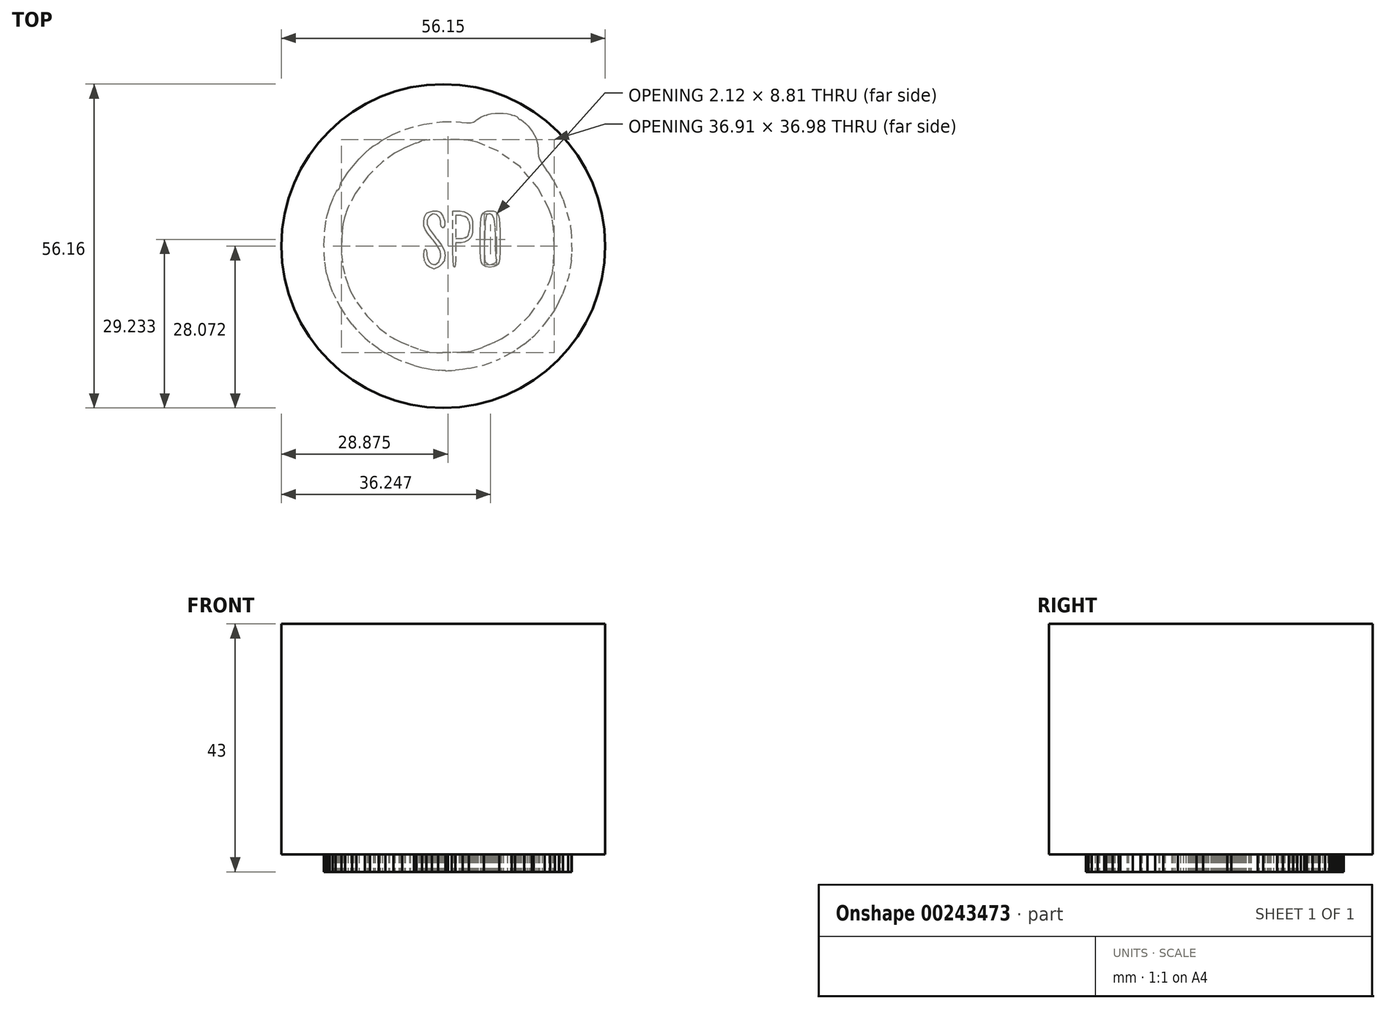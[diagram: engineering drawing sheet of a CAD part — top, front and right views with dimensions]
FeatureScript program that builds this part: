
annotation { "Feature Type Name" : "Feature", "Feature Type Description" : "" }
export const myFeature = defineFeature(function(context is Context, id is Id, definition is map)
    precondition{}
    {
        {
            var Q0;
            Q0=qCreatedBy(makeId("Top.planeOp"),FACE);
            var sketch = newSketch(context, id + "F0", { "sketchPlane" : qUnion([Q0])});
            skLineSegment(sketch, "E0", {"start": v(-1.98, -21.51) * mm, "end": v(-2.83, -21.44) * mm});
            skLineSegment(sketch, "E1", {"start": v(-2.83, -21.44) * mm, "end": v(-5.33, -20.94) * mm});
            skLineSegment(sketch, "E2", {"start": v(-5.33, -20.94) * mm, "end": v(-8.48, -19.86) * mm});
            skLineSegment(sketch, "E3", {"start": v(-8.48, -19.86) * mm, "end": v(-11.41, -18.31) * mm});
            skLineSegment(sketch, "E4", {"start": v(-11.41, -18.31) * mm, "end": v(-14.06, -16.34) * mm});
            skLineSegment(sketch, "E5", {"start": v(-14.06, -16.34) * mm, "end": v(-16.4, -13.97) * mm});
            skLineSegment(sketch, "E6", {"start": v(-16.4, -13.97) * mm, "end": v(-18.36, -11.25) * mm});
            skLineSegment(sketch, "E7", {"start": v(-18.36, -11.25) * mm, "end": v(-19.92, -8.21) * mm});
            skLineSegment(sketch, "E8", {"start": v(-19.92, -8.21) * mm, "end": v(-20.82, -5.74) * mm});
            skLineSegment(sketch, "E9", {"start": v(-20.82, -5.74) * mm, "end": v(-21.03, -4.9) * mm});
            skLineSegment(sketch, "E10", {"start": v(-21.03, -4.9) * mm, "end": v(-21.18, -4.33) * mm});
            skLineSegment(sketch, "E11", {"start": v(-21.18, -4.33) * mm, "end": v(-21.41, -2.57) * mm});
            skLineSegment(sketch, "E12", {"start": v(-21.41, -2.57) * mm, "end": v(-21.52, 0.18) * mm});
            skLineSegment(sketch, "E13", {"start": v(-21.52, 0.18) * mm, "end": v(-21.37, 2.94) * mm});
            skLineSegment(sketch, "E14", {"start": v(-21.37, 2.94) * mm, "end": v(-21.1, 4.72) * mm});
            skLineSegment(sketch, "E15", {"start": v(-21.1, 4.72) * mm, "end": v(-20.95, 5.3) * mm});
            skLineSegment(sketch, "E16", {"start": v(-20.95, 5.3) * mm, "end": v(-20.84, 5.71) * mm});
            skLineSegment(sketch, "E17", {"start": v(-20.84, 5.71) * mm, "end": v(-20.44, 6.97) * mm});
            skLineSegment(sketch, "E18", {"start": v(-20.44, 6.97) * mm, "end": v(-19.9, 8.4) * mm});
            skLineSegment(sketch, "E19", {"start": v(-19.9, 8.4) * mm, "end": v(-19.4, 9.41) * mm});
            skLineSegment(sketch, "E20", {"start": v(-19.4, 9.41) * mm, "end": v(-19.14, 9.79) * mm});
            skLineSegment(sketch, "E21", {"start": v(-19.14, 9.79) * mm, "end": v(-19.05, 9.79) * mm});
            skLineSegment(sketch, "E22", {"start": v(-19.05, 9.79) * mm, "end": v(-19, 9.79) * mm});
            skLineSegment(sketch, "E23", {"start": v(-19, 9.79) * mm, "end": v(-18.86, 9.93) * mm});
            skLineSegment(sketch, "E24", {"start": v(-18.86, 9.93) * mm, "end": v(-18.79, 10.18) * mm});
            skLineSegment(sketch, "E25", {"start": v(-18.79, 10.18) * mm, "end": v(-18.79, 10.27) * mm});
            skLineSegment(sketch, "E26", {"start": v(-18.79, 10.27) * mm, "end": v(-18.79, 10.42) * mm});
            skLineSegment(sketch, "E27", {"start": v(-18.79, 10.42) * mm, "end": v(-18.6, 10.87) * mm});
            skLineSegment(sketch, "E28", {"start": v(-18.6, 10.87) * mm, "end": v(-18.09, 11.76) * mm});
            skLineSegment(sketch, "E29", {"start": v(-18.09, 11.76) * mm, "end": v(-17.33, 12.83) * mm});
            skLineSegment(sketch, "E30", {"start": v(-17.33, 12.83) * mm, "end": v(-16.42, 13.97) * mm});
            skLineSegment(sketch, "E31", {"start": v(-16.42, 13.97) * mm, "end": v(-15.42, 15.1) * mm});
            skLineSegment(sketch, "E32", {"start": v(-15.42, 15.1) * mm, "end": v(-14.43, 16.13) * mm});
            skLineSegment(sketch, "E33", {"start": v(-14.43, 16.13) * mm, "end": v(-13.52, 16.95) * mm});
            skLineSegment(sketch, "E34", {"start": v(-13.52, 16.95) * mm, "end": v(-12.98, 17.36) * mm});
            skLineSegment(sketch, "E35", {"start": v(-12.98, 17.36) * mm, "end": v(-12.78, 17.46) * mm});
            skLineSegment(sketch, "E36", {"start": v(-12.78, 17.46) * mm, "end": v(-12.68, 17.52) * mm});
            skLineSegment(sketch, "E37", {"start": v(-12.68, 17.52) * mm, "end": v(-12.22, 17.8) * mm});
            skLineSegment(sketch, "E38", {"start": v(-12.22, 17.8) * mm, "end": v(-11.93, 18) * mm});
            skLineSegment(sketch, "E39", {"start": v(-11.93, 18) * mm, "end": v(-11.9, 18.02) * mm});
            skLineSegment(sketch, "E40", {"start": v(-11.9, 18.02) * mm, "end": v(-11.89, 18.05) * mm});
            skLineSegment(sketch, "E41", {"start": v(-11.89, 18.05) * mm, "end": v(-11.74, 18.15) * mm});
            skLineSegment(sketch, "E42", {"start": v(-11.74, 18.15) * mm, "end": v(-11.38, 18.38) * mm});
            skLineSegment(sketch, "E43", {"start": v(-11.38, 18.38) * mm, "end": v(-10.9, 18.67) * mm});
            skLineSegment(sketch, "E44", {"start": v(-10.9, 18.67) * mm, "end": v(-10.46, 18.92) * mm});
            skLineSegment(sketch, "E45", {"start": v(-10.46, 18.92) * mm, "end": v(-10.32, 19) * mm});
            skLineSegment(sketch, "E46", {"start": v(-10.32, 19) * mm, "end": v(-9.64, 19.38) * mm});
            skLineSegment(sketch, "E47", {"start": v(-9.64, 19.38) * mm, "end": v(-7.46, 20.26) * mm});
            skLineSegment(sketch, "E48", {"start": v(-7.46, 20.26) * mm, "end": v(-4.24, 21.13) * mm});
            skLineSegment(sketch, "E49", {"start": v(-4.24, 21.13) * mm, "end": v(-0.95, 21.56) * mm});
            skLineSegment(sketch, "E50", {"start": v(-0.95, 21.56) * mm, "end": v(1.36, 21.58) * mm});
            skLineSegment(sketch, "E51", {"start": v(1.36, 21.58) * mm, "end": v(2.12, 21.48) * mm});
            skLineSegment(sketch, "E52", {"start": v(2.12, 21.48) * mm, "end": v(2.4, 21.45) * mm});
            skLineSegment(sketch, "E53", {"start": v(2.4, 21.45) * mm, "end": v(3.24, 21.36) * mm});
            skLineSegment(sketch, "E54", {"start": v(3.24, 21.36) * mm, "end": v(3.94, 21.37) * mm});
            skLineSegment(sketch, "E55", {"start": v(3.94, 21.37) * mm, "end": v(4.43, 21.53) * mm});
            skLineSegment(sketch, "E56", {"start": v(4.43, 21.53) * mm, "end": v(4.82, 21.79) * mm});
            skLineSegment(sketch, "E57", {"start": v(4.82, 21.79) * mm, "end": v(4.95, 21.88) * mm});
            skLineSegment(sketch, "E58", {"start": v(4.95, 21.88) * mm, "end": v(5.07, 21.97) * mm});
            skLineSegment(sketch, "E59", {"start": v(5.07, 21.97) * mm, "end": v(5.69, 22.37) * mm});
            skLineSegment(sketch, "E60", {"start": v(5.69, 22.37) * mm, "end": v(6.2, 22.6) * mm});
            skLineSegment(sketch, "E61", {"start": v(6.2, 22.6) * mm, "end": v(6.27, 22.62) * mm});
            skLineSegment(sketch, "E62", {"start": v(6.27, 22.62) * mm, "end": v(6.34, 22.64) * mm});
            skLineSegment(sketch, "E63", {"start": v(6.34, 22.64) * mm, "end": v(6.6, 22.7) * mm});
            skLineSegment(sketch, "E64", {"start": v(6.6, 22.7) * mm, "end": v(6.75, 22.74) * mm});
            skLineSegment(sketch, "E65", {"start": v(6.75, 22.74) * mm, "end": v(6.75, 22.75) * mm});
            skLineSegment(sketch, "E66", {"start": v(6.75, 22.75) * mm, "end": v(6.75, 22.78) * mm});
            skLineSegment(sketch, "E67", {"start": v(6.75, 22.78) * mm, "end": v(6.95, 22.86) * mm});
            skLineSegment(sketch, "E68", {"start": v(6.95, 22.86) * mm, "end": v(7.47, 22.95) * mm});
            skLineSegment(sketch, "E69", {"start": v(7.47, 22.95) * mm, "end": v(8.15, 23.02) * mm});
            skLineSegment(sketch, "E70", {"start": v(8.15, 23.02) * mm, "end": v(8.69, 23.04) * mm});
            skLineSegment(sketch, "E71", {"start": v(8.69, 23.04) * mm, "end": v(8.86, 23.04) * mm});
            skLineSegment(sketch, "E72", {"start": v(8.86, 23.04) * mm, "end": v(9.04, 23.04) * mm});
            skLineSegment(sketch, "E73", {"start": v(9.04, 23.04) * mm, "end": v(9.57, 23.02) * mm});
            skLineSegment(sketch, "E74", {"start": v(9.57, 23.02) * mm, "end": v(10.26, 22.95) * mm});
            skLineSegment(sketch, "E75", {"start": v(10.26, 22.95) * mm, "end": v(10.77, 22.86) * mm});
            skLineSegment(sketch, "E76", {"start": v(10.77, 22.86) * mm, "end": v(10.98, 22.78) * mm});
            skLineSegment(sketch, "E77", {"start": v(10.98, 22.78) * mm, "end": v(10.98, 22.75) * mm});
            skLineSegment(sketch, "E78", {"start": v(10.98, 22.75) * mm, "end": v(10.98, 22.74) * mm});
            skLineSegment(sketch, "E79", {"start": v(10.98, 22.74) * mm, "end": v(11.13, 22.7) * mm});
            skLineSegment(sketch, "E80", {"start": v(11.13, 22.7) * mm, "end": v(11.44, 22.64) * mm});
            skLineSegment(sketch, "E81", {"start": v(11.44, 22.64) * mm, "end": v(11.5, 22.62) * mm});
            skLineSegment(sketch, "E82", {"start": v(11.5, 22.62) * mm, "end": v(11.58, 22.6) * mm});
            skLineSegment(sketch, "E83", {"start": v(11.58, 22.6) * mm, "end": v(11.9, 22.47) * mm});
            skLineSegment(sketch, "E84", {"start": v(11.9, 22.47) * mm, "end": v(12.1, 22.28) * mm});
            skLineSegment(sketch, "E85", {"start": v(12.1, 22.28) * mm, "end": v(12.12, 22.25) * mm});
            skLineSegment(sketch, "E86", {"start": v(12.12, 22.25) * mm, "end": v(12.13, 22.21) * mm});
            skLineSegment(sketch, "E87", {"start": v(12.13, 22.21) * mm, "end": v(12.26, 22.05) * mm});
            skLineSegment(sketch, "E88", {"start": v(12.26, 22.05) * mm, "end": v(12.43, 21.96) * mm});
            skLineSegment(sketch, "E89", {"start": v(12.43, 21.96) * mm, "end": v(12.49, 21.96) * mm});
            skLineSegment(sketch, "E90", {"start": v(12.49, 21.96) * mm, "end": v(12.53, 21.96) * mm});
            skLineSegment(sketch, "E91", {"start": v(12.53, 21.96) * mm, "end": v(12.67, 21.87) * mm});
            skLineSegment(sketch, "E92", {"start": v(12.67, 21.87) * mm, "end": v(13, 21.62) * mm});
            skLineSegment(sketch, "E93", {"start": v(13, 21.62) * mm, "end": v(13.4, 21.25) * mm});
            skLineSegment(sketch, "E94", {"start": v(13.4, 21.25) * mm, "end": v(13.75, 20.91) * mm});
            skLineSegment(sketch, "E95", {"start": v(13.75, 20.91) * mm, "end": v(13.86, 20.8) * mm});
            skLineSegment(sketch, "E96", {"start": v(13.86, 20.8) * mm, "end": v(14.08, 20.57) * mm});
            skLineSegment(sketch, "E97", {"start": v(14.08, 20.57) * mm, "end": v(14.66, 19.81) * mm});
            skLineSegment(sketch, "E98", {"start": v(14.66, 19.81) * mm, "end": v(15.2, 18.77) * mm});
            skLineSegment(sketch, "E99", {"start": v(15.2, 18.77) * mm, "end": v(15.51, 17.62) * mm});
            skLineSegment(sketch, "E100", {"start": v(15.51, 17.62) * mm, "end": v(15.61, 16.65) * mm});
            skLineSegment(sketch, "E101", {"start": v(15.61, 16.65) * mm, "end": v(15.61, 16.32) * mm});
            skLineSegment(sketch, "E102", {"start": v(15.61, 16.32) * mm, "end": v(15.61, 16.15) * mm});
            skLineSegment(sketch, "E103", {"start": v(15.61, 16.15) * mm, "end": v(15.66, 15.63) * mm});
            skLineSegment(sketch, "E104", {"start": v(15.66, 15.63) * mm, "end": v(15.85, 15) * mm});
            skLineSegment(sketch, "E105", {"start": v(15.85, 15) * mm, "end": v(16.28, 14.27) * mm});
            skLineSegment(sketch, "E106", {"start": v(16.28, 14.27) * mm, "end": v(16.82, 13.5) * mm});
            skLineSegment(sketch, "E107", {"start": v(16.82, 13.5) * mm, "end": v(17.01, 13.26) * mm});
            skLineSegment(sketch, "E108", {"start": v(17.01, 13.26) * mm, "end": v(17.84, 12.16) * mm});
            skLineSegment(sketch, "E109", {"start": v(17.84, 12.16) * mm, "end": v(19.8, 8.47) * mm});
            skLineSegment(sketch, "E110", {"start": v(19.8, 8.47) * mm, "end": v(21.3, 3.36) * mm});
            skLineSegment(sketch, "E111", {"start": v(21.3, 3.36) * mm, "end": v(21.48, -1.94) * mm});
            skLineSegment(sketch, "E112", {"start": v(21.48, -1.94) * mm, "end": v(20.77, -6) * mm});
            skLineSegment(sketch, "E113", {"start": v(20.77, -6) * mm, "end": v(20.32, -7.28) * mm});
            skLineSegment(sketch, "E114", {"start": v(20.32, -7.28) * mm, "end": v(20.16, -7.73) * mm});
            skLineSegment(sketch, "E115", {"start": v(20.16, -7.73) * mm, "end": v(19.56, -9.04) * mm});
            skLineSegment(sketch, "E116", {"start": v(19.56, -9.04) * mm, "end": v(18.5, -10.99) * mm});
            skLineSegment(sketch, "E117", {"start": v(18.5, -10.99) * mm, "end": v(17.3, -12.88) * mm});
            skLineSegment(sketch, "E118", {"start": v(17.3, -12.88) * mm, "end": v(16.4, -14.08) * mm});
            skLineSegment(sketch, "E119", {"start": v(16.4, -14.08) * mm, "end": v(16.06, -14.45) * mm});
            skLineSegment(sketch, "E120", {"start": v(16.06, -14.45) * mm, "end": v(15.57, -15) * mm});
            skLineSegment(sketch, "E121", {"start": v(15.57, -15) * mm, "end": v(13.9, -16.5) * mm});
            skLineSegment(sketch, "E122", {"start": v(13.9, -16.5) * mm, "end": v(11.35, -18.33) * mm});
            skLineSegment(sketch, "E123", {"start": v(11.35, -18.33) * mm, "end": v(8.63, -19.79) * mm});
            skLineSegment(sketch, "E124", {"start": v(8.63, -19.79) * mm, "end": v(6.64, -20.57) * mm});
            skLineSegment(sketch, "E125", {"start": v(6.64, -20.57) * mm, "end": v(5.95, -20.74) * mm});
            skLineSegment(sketch, "E126", {"start": v(5.95, -20.74) * mm, "end": v(5.57, -20.85) * mm});
            skLineSegment(sketch, "E127", {"start": v(5.57, -20.85) * mm, "end": v(4.4, -21.08) * mm});
            skLineSegment(sketch, "E128", {"start": v(4.4, -21.08) * mm, "end": v(2.5, -21.4) * mm});
            skLineSegment(sketch, "E129", {"start": v(2.5, -21.4) * mm, "end": v(0.74, -21.6) * mm});
            skLineSegment(sketch, "E130", {"start": v(0.74, -21.6) * mm, "end": v(-0.17, -21.66) * mm});
            skLineSegment(sketch, "E131", {"start": v(-0.17, -21.66) * mm, "end": v(-0.4, -21.64) * mm});
            skLineSegment(sketch, "E132", {"start": v(-0.4, -21.64) * mm, "end": v(-0.47, -21.64) * mm});
            skLineSegment(sketch, "E133", {"start": v(-0.47, -21.64) * mm, "end": v(-1.08, -21.59) * mm});
            skLineSegment(sketch, "E134", {"start": v(-1.08, -21.59) * mm, "end": v(-1.84, -21.52) * mm});
            skLineSegment(sketch, "E135", {"start": v(-1.84, -21.52) * mm, "end": v(-1.98, -21.51) * mm});
            skLineSegment(sketch, "E136", {"start": v(4.37, -18.12) * mm, "end": v(4.57, -18.07) * mm});
            skLineSegment(sketch, "E137", {"start": v(4.57, -18.07) * mm, "end": v(5.18, -17.87) * mm});
            skLineSegment(sketch, "E138", {"start": v(5.18, -17.87) * mm, "end": v(6.23, -17.48) * mm});
            skLineSegment(sketch, "E139", {"start": v(6.23, -17.48) * mm, "end": v(7.37, -17) * mm});
            skLineSegment(sketch, "E140", {"start": v(7.37, -17) * mm, "end": v(8.2, -16.62) * mm});
            skLineSegment(sketch, "E141", {"start": v(8.2, -16.62) * mm, "end": v(8.47, -16.48) * mm});
            skLineSegment(sketch, "E142", {"start": v(8.47, -16.48) * mm, "end": v(9.28, -16.09) * mm});
            skLineSegment(sketch, "E143", {"start": v(9.28, -16.09) * mm, "end": v(11.53, -14.55) * mm});
            skLineSegment(sketch, "E144", {"start": v(11.53, -14.55) * mm, "end": v(14.16, -12) * mm});
            skLineSegment(sketch, "E145", {"start": v(14.16, -12) * mm, "end": v(16.3, -8.9) * mm});
            skLineSegment(sketch, "E146", {"start": v(16.3, -8.9) * mm, "end": v(17.57, -6.22) * mm});
            skLineSegment(sketch, "E147", {"start": v(17.57, -6.22) * mm, "end": v(17.89, -5.3) * mm});
            skLineSegment(sketch, "E148", {"start": v(17.89, -5.3) * mm, "end": v(18.06, -4.77) * mm});
            skLineSegment(sketch, "E149", {"start": v(18.06, -4.77) * mm, "end": v(18.29, -3.05) * mm});
            skLineSegment(sketch, "E150", {"start": v(18.29, -3.05) * mm, "end": v(18.42, 0) * mm});
            skLineSegment(sketch, "E151", {"start": v(18.42, 0) * mm, "end": v(18.29, 3.05) * mm});
            skLineSegment(sketch, "E152", {"start": v(18.29, 3.05) * mm, "end": v(18.06, 4.77) * mm});
            skLineSegment(sketch, "E153", {"start": v(18.06, 4.77) * mm, "end": v(17.89, 5.3) * mm});
            skLineSegment(sketch, "E154", {"start": v(17.89, 5.3) * mm, "end": v(17.47, 6.5) * mm});
            skLineSegment(sketch, "E155", {"start": v(17.47, 6.5) * mm, "end": v(15.64, 9.96) * mm});
            skLineSegment(sketch, "E156", {"start": v(15.64, 9.96) * mm, "end": v(12.48, 13.75) * mm});
            skLineSegment(sketch, "E157", {"start": v(12.48, 13.75) * mm, "end": v(8.5, 16.55) * mm});
            skLineSegment(sketch, "E158", {"start": v(8.5, 16.55) * mm, "end": v(5.04, 17.98) * mm});
            skLineSegment(sketch, "E159", {"start": v(5.04, 17.98) * mm, "end": v(3.84, 18.26) * mm});
            skLineSegment(sketch, "E160", {"start": v(3.84, 18.26) * mm, "end": v(3.45, 18.35) * mm});
            skLineSegment(sketch, "E161", {"start": v(3.45, 18.35) * mm, "end": v(1.91, 18.45) * mm});
            skLineSegment(sketch, "E162", {"start": v(1.91, 18.45) * mm, "end": v(-0.83, 18.48) * mm});
            skLineSegment(sketch, "E163", {"start": v(-0.83, 18.48) * mm, "end": v(-3.38, 18.38) * mm});
            skLineSegment(sketch, "E164", {"start": v(-3.38, 18.38) * mm, "end": v(-4.58, 18.24) * mm});
            skLineSegment(sketch, "E165", {"start": v(-4.58, 18.24) * mm, "end": v(-4.71, 18.15) * mm});
            skLineSegment(sketch, "E166", {"start": v(-4.71, 18.15) * mm, "end": v(-4.76, 18.11) * mm});
            skLineSegment(sketch, "E167", {"start": v(-4.76, 18.11) * mm, "end": v(-5.13, 17.94) * mm});
            skLineSegment(sketch, "E168", {"start": v(-5.13, 17.94) * mm, "end": v(-5.54, 17.82) * mm});
            skLineSegment(sketch, "E169", {"start": v(-5.54, 17.82) * mm, "end": v(-5.6, 17.8) * mm});
            skLineSegment(sketch, "E170", {"start": v(-5.6, 17.8) * mm, "end": v(-5.68, 17.8) * mm});
            skLineSegment(sketch, "E171", {"start": v(-5.68, 17.8) * mm, "end": v(-6, 17.67) * mm});
            skLineSegment(sketch, "E172", {"start": v(-6, 17.67) * mm, "end": v(-6.69, 17.38) * mm});
            skLineSegment(sketch, "E173", {"start": v(-6.69, 17.38) * mm, "end": v(-7.56, 16.97) * mm});
            skLineSegment(sketch, "E174", {"start": v(-7.56, 16.97) * mm, "end": v(-8.28, 16.61) * mm});
            skLineSegment(sketch, "E175", {"start": v(-8.28, 16.61) * mm, "end": v(-8.52, 16.48) * mm});
            skLineSegment(sketch, "E176", {"start": v(-8.52, 16.48) * mm, "end": v(-9.27, 16.1) * mm});
            skLineSegment(sketch, "E177", {"start": v(-9.27, 16.1) * mm, "end": v(-11.37, 14.6) * mm});
            skLineSegment(sketch, "E178", {"start": v(-11.37, 14.6) * mm, "end": v(-13.94, 12.1) * mm});
            skLineSegment(sketch, "E179", {"start": v(-13.94, 12.1) * mm, "end": v(-16.1, 9.13) * mm});
            skLineSegment(sketch, "E180", {"start": v(-16.1, 9.13) * mm, "end": v(-17.36, 6.72) * mm});
            skLineSegment(sketch, "E181", {"start": v(-17.36, 6.72) * mm, "end": v(-17.67, 5.87) * mm});
            skLineSegment(sketch, "E182", {"start": v(-17.67, 5.87) * mm, "end": v(-17.77, 5.62) * mm});
            skLineSegment(sketch, "E183", {"start": v(-17.77, 5.62) * mm, "end": v(-18, 4.85) * mm});
            skLineSegment(sketch, "E184", {"start": v(-18, 4.85) * mm, "end": v(-18.23, 3.81) * mm});
            skLineSegment(sketch, "E185", {"start": v(-18.23, 3.81) * mm, "end": v(-18.37, 2.56) * mm});
            skLineSegment(sketch, "E186", {"start": v(-18.37, 2.56) * mm, "end": v(-18.45, 1.31) * mm});
            skLineSegment(sketch, "E187", {"start": v(-18.45, 1.31) * mm, "end": v(-18.47, 0.9) * mm});
            skLineSegment(sketch, "E188", {"start": v(-18.47, 0.9) * mm, "end": v(-18.5, 0.33) * mm});
            skLineSegment(sketch, "E189", {"start": v(-18.5, 0.33) * mm, "end": v(-18.48, -1.4) * mm});
            skLineSegment(sketch, "E190", {"start": v(-18.48, -1.4) * mm, "end": v(-18.28, -3.38) * mm});
            skLineSegment(sketch, "E191", {"start": v(-18.28, -3.38) * mm, "end": v(-17.85, -5.26) * mm});
            skLineSegment(sketch, "E192", {"start": v(-17.85, -5.26) * mm, "end": v(-17.34, -6.78) * mm});
            skLineSegment(sketch, "E193", {"start": v(-17.34, -6.78) * mm, "end": v(-17.15, -7.28) * mm});
            skLineSegment(sketch, "E194", {"start": v(-17.15, -7.28) * mm, "end": v(-16.9, -7.92) * mm});
            skLineSegment(sketch, "E195", {"start": v(-16.9, -7.92) * mm, "end": v(-15.87, -9.74) * mm});
            skLineSegment(sketch, "E196", {"start": v(-15.87, -9.74) * mm, "end": v(-14.05, -12.14) * mm});
            skLineSegment(sketch, "E197", {"start": v(-14.05, -12.14) * mm, "end": v(-11.88, -14.3) * mm});
            skLineSegment(sketch, "E198", {"start": v(-11.88, -14.3) * mm, "end": v(-10.15, -15.62) * mm});
            skLineSegment(sketch, "E199", {"start": v(-10.15, -15.62) * mm, "end": v(-9.53, -15.98) * mm});
            skLineSegment(sketch, "E200", {"start": v(-9.53, -15.98) * mm, "end": v(-9.2, -16.17) * mm});
            skLineSegment(sketch, "E201", {"start": v(-9.2, -16.17) * mm, "end": v(-8.2, -16.65) * mm});
            skLineSegment(sketch, "E202", {"start": v(-8.2, -16.65) * mm, "end": v(-6.57, -17.36) * mm});
            skLineSegment(sketch, "E203", {"start": v(-6.57, -17.36) * mm, "end": v(-4.92, -17.96) * mm});
            skLineSegment(sketch, "E204", {"start": v(-4.92, -17.96) * mm, "end": v(-3.91, -18.27) * mm});
            skLineSegment(sketch, "E205", {"start": v(-3.91, -18.27) * mm, "end": v(-3.57, -18.34) * mm});
            skLineSegment(sketch, "E206", {"start": v(-3.57, -18.34) * mm, "end": v(-3.24, -18.4) * mm});
            skLineSegment(sketch, "E207", {"start": v(-3.24, -18.4) * mm, "end": v(-1.97, -18.48) * mm});
            skLineSegment(sketch, "E208", {"start": v(-1.97, -18.48) * mm, "end": v(0.36, -18.48) * mm});
            skLineSegment(sketch, "E209", {"start": v(0.36, -18.48) * mm, "end": v(2.7, -18.35) * mm});
            skLineSegment(sketch, "E210", {"start": v(2.7, -18.35) * mm, "end": v(4, -18.22) * mm});
            skLineSegment(sketch, "E211", {"start": v(4, -18.22) * mm, "end": v(4.37, -18.12) * mm});
            skLineSegment(sketch, "E212", {"start": v(-2.91, -3.78) * mm, "end": v(-3.07, -3.72) * mm});
            skLineSegment(sketch, "E213", {"start": v(-3.07, -3.72) * mm, "end": v(-3.5, -3.47) * mm});
            skLineSegment(sketch, "E214", {"start": v(-3.5, -3.47) * mm, "end": v(-3.92, -3.02) * mm});
            skLineSegment(sketch, "E215", {"start": v(-3.92, -3.02) * mm, "end": v(-4.16, -2.43) * mm});
            skLineSegment(sketch, "E216", {"start": v(-4.16, -2.43) * mm, "end": v(-4.23, -1.86) * mm});
            skLineSegment(sketch, "E217", {"start": v(-4.23, -1.86) * mm, "end": v(-4.23, -1.67) * mm});
            skLineSegment(sketch, "E218", {"start": v(-4.23, -1.67) * mm, "end": v(-4.23, -1.47) * mm});
            skLineSegment(sketch, "E219", {"start": v(-4.23, -1.47) * mm, "end": v(-4.15, -0.87) * mm});
            skLineSegment(sketch, "E220", {"start": v(-4.15, -0.87) * mm, "end": v(-4.01, -0.53) * mm});
            skLineSegment(sketch, "E221", {"start": v(-4.01, -0.53) * mm, "end": v(-3.97, -0.53) * mm});
            skLineSegment(sketch, "E222", {"start": v(-3.97, -0.53) * mm, "end": v(-3.92, -0.53) * mm});
            skLineSegment(sketch, "E223", {"start": v(-3.92, -0.53) * mm, "end": v(-3.78, -0.79) * mm});
            skLineSegment(sketch, "E224", {"start": v(-3.78, -0.79) * mm, "end": v(-3.7, -1.27) * mm});
            skLineSegment(sketch, "E225", {"start": v(-3.7, -1.27) * mm, "end": v(-3.7, -1.43) * mm});
            skLineSegment(sketch, "E226", {"start": v(-3.7, -1.43) * mm, "end": v(-3.7, -1.6) * mm});
            skLineSegment(sketch, "E227", {"start": v(-3.7, -1.6) * mm, "end": v(-3.6, -2.11) * mm});
            skLineSegment(sketch, "E228", {"start": v(-3.6, -2.11) * mm, "end": v(-3.33, -2.67) * mm});
            skLineSegment(sketch, "E229", {"start": v(-3.33, -2.67) * mm, "end": v(-2.92, -3.04) * mm});
            skLineSegment(sketch, "E230", {"start": v(-2.92, -3.04) * mm, "end": v(-2.54, -3.18) * mm});
            skLineSegment(sketch, "E231", {"start": v(-2.54, -3.18) * mm, "end": v(-2.4, -3.18) * mm});
            skLineSegment(sketch, "E232", {"start": v(-2.4, -3.18) * mm, "end": v(-2.2, -3.18) * mm});
            skLineSegment(sketch, "E233", {"start": v(-2.2, -3.18) * mm, "end": v(-1.6, -2.76) * mm});
            skLineSegment(sketch, "E234", {"start": v(-1.6, -2.76) * mm, "end": v(-1.32, -1.86) * mm});
            skLineSegment(sketch, "E235", {"start": v(-1.32, -1.86) * mm, "end": v(-1.32, -1.56) * mm});
            skLineSegment(sketch, "E236", {"start": v(-1.32, -1.56) * mm, "end": v(-1.32, -1.42) * mm});
            skLineSegment(sketch, "E237", {"start": v(-1.32, -1.42) * mm, "end": v(-1.38, -1) * mm});
            skLineSegment(sketch, "E238", {"start": v(-1.38, -1) * mm, "end": v(-1.6, -0.42) * mm});
            skLineSegment(sketch, "E239", {"start": v(-1.6, -0.42) * mm, "end": v(-2.05, 0.27) * mm});
            skLineSegment(sketch, "E240", {"start": v(-2.05, 0.27) * mm, "end": v(-2.6, 0.97) * mm});
            skLineSegment(sketch, "E241", {"start": v(-2.6, 0.97) * mm, "end": v(-2.78, 1.2) * mm});
            skLineSegment(sketch, "E242", {"start": v(-2.78, 1.2) * mm, "end": v(-2.97, 1.43) * mm});
            skLineSegment(sketch, "E243", {"start": v(-2.97, 1.43) * mm, "end": v(-3.53, 2.16) * mm});
            skLineSegment(sketch, "E244", {"start": v(-3.53, 2.16) * mm, "end": v(-3.97, 2.86) * mm});
            skLineSegment(sketch, "E245", {"start": v(-3.97, 2.86) * mm, "end": v(-4.18, 3.45) * mm});
            skLineSegment(sketch, "E246", {"start": v(-4.18, 3.45) * mm, "end": v(-4.23, 3.94) * mm});
            skLineSegment(sketch, "E247", {"start": v(-4.23, 3.94) * mm, "end": v(-4.23, 4.1) * mm});
            skLineSegment(sketch, "E248", {"start": v(-4.23, 4.1) * mm, "end": v(-4.23, 4.34) * mm});
            skLineSegment(sketch, "E249", {"start": v(-4.23, 4.34) * mm, "end": v(-4.11, 5.04) * mm});
            skLineSegment(sketch, "E250", {"start": v(-4.11, 5.04) * mm, "end": v(-3.84, 5.56) * mm});
            skLineSegment(sketch, "E251", {"start": v(-3.84, 5.56) * mm, "end": v(-3.76, 5.64) * mm});
            skLineSegment(sketch, "E252", {"start": v(-3.76, 5.64) * mm, "end": v(-3.65, 5.73) * mm});
            skLineSegment(sketch, "E253", {"start": v(-3.65, 5.73) * mm, "end": v(-3.26, 5.91) * mm});
            skLineSegment(sketch, "E254", {"start": v(-3.26, 5.91) * mm, "end": v(-2.6, 6.05) * mm});
            skLineSegment(sketch, "E255", {"start": v(-2.6, 6.05) * mm, "end": v(-1.95, 6.05) * mm});
            skLineSegment(sketch, "E256", {"start": v(-1.95, 6.05) * mm, "end": v(-1.54, 5.94) * mm});
            skLineSegment(sketch, "E257", {"start": v(-1.54, 5.94) * mm, "end": v(-1.43, 5.87) * mm});
            skLineSegment(sketch, "E258", {"start": v(-1.43, 5.87) * mm, "end": v(-1.26, 5.76) * mm});
            skLineSegment(sketch, "E259", {"start": v(-1.26, 5.76) * mm, "end": v(-0.89, 5.22) * mm});
            skLineSegment(sketch, "E260", {"start": v(-0.89, 5.22) * mm, "end": v(-0.58, 4.32) * mm});
            skLineSegment(sketch, "E261", {"start": v(-0.58, 4.32) * mm, "end": v(-0.57, 3.52) * mm});
            skLineSegment(sketch, "E262", {"start": v(-0.57, 3.52) * mm, "end": v(-0.84, 3.17) * mm});
            skLineSegment(sketch, "E263", {"start": v(-0.84, 3.17) * mm, "end": v(-0.93, 3.17) * mm});
            skLineSegment(sketch, "E264", {"start": v(-0.93, 3.17) * mm, "end": v(-1, 3.17) * mm});
            skLineSegment(sketch, "E265", {"start": v(-1, 3.17) * mm, "end": v(-1.22, 3.38) * mm});
            skLineSegment(sketch, "E266", {"start": v(-1.22, 3.38) * mm, "end": v(-1.32, 3.88) * mm});
            skLineSegment(sketch, "E267", {"start": v(-1.32, 3.88) * mm, "end": v(-1.32, 4.05) * mm});
            skLineSegment(sketch, "E268", {"start": v(-1.32, 4.05) * mm, "end": v(-1.32, 4.27) * mm});
            skLineSegment(sketch, "E269", {"start": v(-1.32, 4.27) * mm, "end": v(-1.5, 4.94) * mm});
            skLineSegment(sketch, "E270", {"start": v(-1.5, 4.94) * mm, "end": v(-1.97, 5.46) * mm});
            skLineSegment(sketch, "E271", {"start": v(-1.97, 5.46) * mm, "end": v(-2.6, 5.55) * mm});
            skLineSegment(sketch, "E272", {"start": v(-2.6, 5.55) * mm, "end": v(-3.15, 5.27) * mm});
            skLineSegment(sketch, "E273", {"start": v(-3.15, 5.27) * mm, "end": v(-3.28, 5.13) * mm});
            skLineSegment(sketch, "E274", {"start": v(-3.28, 5.13) * mm, "end": v(-3.4, 5) * mm});
            skLineSegment(sketch, "E275", {"start": v(-3.4, 5) * mm, "end": v(-3.66, 4.52) * mm});
            skLineSegment(sketch, "E276", {"start": v(-3.66, 4.52) * mm, "end": v(-3.61, 3.75) * mm});
            skLineSegment(sketch, "E277", {"start": v(-3.61, 3.75) * mm, "end": v(-3.11, 2.75) * mm});
            skLineSegment(sketch, "E278", {"start": v(-3.11, 2.75) * mm, "end": v(-2.38, 1.73) * mm});
            skLineSegment(sketch, "E279", {"start": v(-2.38, 1.73) * mm, "end": v(-2.12, 1.4) * mm});
            skLineSegment(sketch, "E280", {"start": v(-2.12, 1.4) * mm, "end": v(-1.87, 1.1) * mm});
            skLineSegment(sketch, "E281", {"start": v(-1.87, 1.1) * mm, "end": v(-1.17, 0.15) * mm});
            skLineSegment(sketch, "E282", {"start": v(-1.17, 0.15) * mm, "end": v(-0.67, -0.8) * mm});
            skLineSegment(sketch, "E283", {"start": v(-0.67, -0.8) * mm, "end": v(-0.53, -1.64) * mm});
            skLineSegment(sketch, "E284", {"start": v(-0.53, -1.64) * mm, "end": v(-0.63, -2.36) * mm});
            skLineSegment(sketch, "E285", {"start": v(-0.63, -2.36) * mm, "end": v(-0.69, -2.6) * mm});
            skLineSegment(sketch, "E286", {"start": v(-0.69, -2.6) * mm, "end": v(-0.72, -2.7) * mm});
            skLineSegment(sketch, "E287", {"start": v(-0.72, -2.7) * mm, "end": v(-0.96, -3.02) * mm});
            skLineSegment(sketch, "E288", {"start": v(-0.96, -3.02) * mm, "end": v(-1.47, -3.49) * mm});
            skLineSegment(sketch, "E289", {"start": v(-1.47, -3.49) * mm, "end": v(-2.02, -3.84) * mm});
            skLineSegment(sketch, "E290", {"start": v(-2.02, -3.84) * mm, "end": v(-2.35, -3.97) * mm});
            skLineSegment(sketch, "E291", {"start": v(-2.35, -3.97) * mm, "end": v(-2.43, -3.94) * mm});
            skLineSegment(sketch, "E292", {"start": v(-2.43, -3.94) * mm, "end": v(-2.48, -3.94) * mm});
            skLineSegment(sketch, "E293", {"start": v(-2.48, -3.94) * mm, "end": v(-2.61, -3.9) * mm});
            skLineSegment(sketch, "E294", {"start": v(-2.61, -3.9) * mm, "end": v(-2.86, -3.8) * mm});
            skLineSegment(sketch, "E295", {"start": v(-2.86, -3.8) * mm, "end": v(-2.91, -3.78) * mm});
            skLineSegment(sketch, "E296", {"start": v(-14.47, 1.11) * mm, "end": v(-14.47, 1.67) * mm});
            skLineSegment(sketch, "E297", {"start": v(-14.47, 1.67) * mm, "end": v(-14.44, 3.35) * mm});
            skLineSegment(sketch, "E298", {"start": v(-14.44, 3.35) * mm, "end": v(-14.37, 4.85) * mm});
            skLineSegment(sketch, "E299", {"start": v(-14.37, 4.85) * mm, "end": v(-14.26, 5.7) * mm});
            skLineSegment(sketch, "E300", {"start": v(-14.26, 5.7) * mm, "end": v(-14.16, 5.99) * mm});
            skLineSegment(sketch, "E301", {"start": v(-14.16, 5.99) * mm, "end": v(-14.1, 6) * mm});
            skLineSegment(sketch, "E302", {"start": v(-14.1, 6) * mm, "end": v(-14.08, 6.02) * mm});
            skLineSegment(sketch, "E303", {"start": v(-14.08, 6.02) * mm, "end": v(-13.94, 5.84) * mm});
            skLineSegment(sketch, "E304", {"start": v(-13.94, 5.84) * mm, "end": v(-13.83, 5.12) * mm});
            skLineSegment(sketch, "E305", {"start": v(-13.83, 5.12) * mm, "end": v(-13.75, 3.73) * mm});
            skLineSegment(sketch, "E306", {"start": v(-13.75, 3.73) * mm, "end": v(-13.71, 2.1) * mm});
            skLineSegment(sketch, "E307", {"start": v(-13.71, 2.1) * mm, "end": v(-13.7, 1.56) * mm});
            skLineSegment(sketch, "E308", {"start": v(-13.7, 1.56) * mm, "end": v(-13.63, -3.02) * mm});
            skLineSegment(sketch, "E309", {"start": v(-13.63, -3.02) * mm, "end": v(-12.49, -3) * mm});
            skLineSegment(sketch, "E310", {"start": v(-12.49, -3) * mm, "end": v(-12.29, -2.98) * mm});
            skLineSegment(sketch, "E311", {"start": v(-12.29, -2.98) * mm, "end": v(-11.63, -3.05) * mm});
            skLineSegment(sketch, "E312", {"start": v(-11.63, -3.05) * mm, "end": v(-11.38, -3.26) * mm});
            skLineSegment(sketch, "E313", {"start": v(-11.38, -3.26) * mm, "end": v(-11.38, -3.33) * mm});
            skLineSegment(sketch, "E314", {"start": v(-11.38, -3.33) * mm, "end": v(-11.38, -3.37) * mm});
            skLineSegment(sketch, "E315", {"start": v(-11.38, -3.37) * mm, "end": v(-11.46, -3.5) * mm});
            skLineSegment(sketch, "E316", {"start": v(-11.46, -3.5) * mm, "end": v(-11.72, -3.62) * mm});
            skLineSegment(sketch, "E317", {"start": v(-11.72, -3.62) * mm, "end": v(-12.21, -3.68) * mm});
            skLineSegment(sketch, "E318", {"start": v(-12.21, -3.68) * mm, "end": v(-12.78, -3.7) * mm});
            skLineSegment(sketch, "E319", {"start": v(-12.78, -3.7) * mm, "end": v(-12.96, -3.7) * mm});
            skLineSegment(sketch, "E320", {"start": v(-12.96, -3.7) * mm, "end": v(-14.53, -3.7) * mm});
            skLineSegment(sketch, "E321", {"start": v(-14.53, -3.7) * mm, "end": v(-14.47, 1.11) * mm});
            skLineSegment(sketch, "E322", {"start": v(-10.27, 1.11) * mm, "end": v(-10.19, 5.95) * mm});
            skLineSegment(sketch, "E323", {"start": v(-10.19, 5.95) * mm, "end": v(-8.63, 6.03) * mm});
            skLineSegment(sketch, "E324", {"start": v(-8.63, 6.03) * mm, "end": v(-8.44, 6.04) * mm});
            skLineSegment(sketch, "E325", {"start": v(-8.44, 6.04) * mm, "end": v(-7.9, 6.05) * mm});
            skLineSegment(sketch, "E326", {"start": v(-7.9, 6.05) * mm, "end": v(-7.45, 6.02) * mm});
            skLineSegment(sketch, "E327", {"start": v(-7.45, 6.02) * mm, "end": v(-7.22, 5.93) * mm});
            skLineSegment(sketch, "E328", {"start": v(-7.22, 5.93) * mm, "end": v(-7.19, 5.8) * mm});
            skLineSegment(sketch, "E329", {"start": v(-7.19, 5.8) * mm, "end": v(-7.2, 5.77) * mm});
            skLineSegment(sketch, "E330", {"start": v(-7.2, 5.77) * mm, "end": v(-7.22, 5.72) * mm});
            skLineSegment(sketch, "E331", {"start": v(-7.22, 5.72) * mm, "end": v(-7.63, 5.5) * mm});
            skLineSegment(sketch, "E332", {"start": v(-7.63, 5.5) * mm, "end": v(-8.33, 5.36) * mm});
            skLineSegment(sketch, "E333", {"start": v(-8.33, 5.36) * mm, "end": v(-8.5, 5.34) * mm});
            skLineSegment(sketch, "E334", {"start": v(-8.5, 5.34) * mm, "end": v(-9.66, 5.27) * mm});
            skLineSegment(sketch, "E335", {"start": v(-9.66, 5.27) * mm, "end": v(-9.58, 3.44) * mm});
            skLineSegment(sketch, "E336", {"start": v(-9.58, 3.44) * mm, "end": v(-9.56, 3.17) * mm});
            skLineSegment(sketch, "E337", {"start": v(-9.56, 3.17) * mm, "end": v(-9.5, 2.37) * mm});
            skLineSegment(sketch, "E338", {"start": v(-9.5, 2.37) * mm, "end": v(-9.39, 1.82) * mm});
            skLineSegment(sketch, "E339", {"start": v(-9.39, 1.82) * mm, "end": v(-9.15, 1.62) * mm});
            skLineSegment(sketch, "E340", {"start": v(-9.15, 1.62) * mm, "end": v(-8.82, 1.59) * mm});
            skLineSegment(sketch, "E341", {"start": v(-8.82, 1.59) * mm, "end": v(-8.7, 1.59) * mm});
            skLineSegment(sketch, "E342", {"start": v(-8.7, 1.59) * mm, "end": v(-8.56, 1.59) * mm});
            skLineSegment(sketch, "E343", {"start": v(-8.56, 1.59) * mm, "end": v(-8.13, 1.49) * mm});
            skLineSegment(sketch, "E344", {"start": v(-8.13, 1.49) * mm, "end": v(-7.94, 1.26) * mm});
            skLineSegment(sketch, "E345", {"start": v(-7.94, 1.26) * mm, "end": v(-7.94, 1.2) * mm});
            skLineSegment(sketch, "E346", {"start": v(-7.94, 1.2) * mm, "end": v(-7.94, 1.12) * mm});
            skLineSegment(sketch, "E347", {"start": v(-7.94, 1.12) * mm, "end": v(-8.14, 0.9) * mm});
            skLineSegment(sketch, "E348", {"start": v(-8.14, 0.9) * mm, "end": v(-8.62, 0.8) * mm});
            skLineSegment(sketch, "E349", {"start": v(-8.62, 0.8) * mm, "end": v(-8.78, 0.8) * mm});
            skLineSegment(sketch, "E350", {"start": v(-8.78, 0.8) * mm, "end": v(-9.66, 0.8) * mm});
            skLineSegment(sketch, "E351", {"start": v(-9.66, 0.8) * mm, "end": v(-9.58, -1.14) * mm});
            skLineSegment(sketch, "E352", {"start": v(-9.58, -1.14) * mm, "end": v(-9.5, -3.07) * mm});
            skLineSegment(sketch, "E353", {"start": v(-9.5, -3.07) * mm, "end": v(-8.3, -3.02) * mm});
            skLineSegment(sketch, "E354", {"start": v(-8.3, -3.02) * mm, "end": v(-8.1, -3) * mm});
            skLineSegment(sketch, "E355", {"start": v(-8.1, -3) * mm, "end": v(-7.4, -3.05) * mm});
            skLineSegment(sketch, "E356", {"start": v(-7.4, -3.05) * mm, "end": v(-7.14, -3.26) * mm});
            skLineSegment(sketch, "E357", {"start": v(-7.14, -3.26) * mm, "end": v(-7.14, -3.33) * mm});
            skLineSegment(sketch, "E358", {"start": v(-7.14, -3.33) * mm, "end": v(-7.14, -3.37) * mm});
            skLineSegment(sketch, "E359", {"start": v(-7.14, -3.37) * mm, "end": v(-7.23, -3.5) * mm});
            skLineSegment(sketch, "E360", {"start": v(-7.23, -3.5) * mm, "end": v(-7.5, -3.62) * mm});
            skLineSegment(sketch, "E361", {"start": v(-7.5, -3.62) * mm, "end": v(-7.98, -3.68) * mm});
            skLineSegment(sketch, "E362", {"start": v(-7.98, -3.68) * mm, "end": v(-8.54, -3.7) * mm});
            skLineSegment(sketch, "E363", {"start": v(-8.54, -3.7) * mm, "end": v(-8.73, -3.7) * mm});
            skLineSegment(sketch, "E364", {"start": v(-8.73, -3.7) * mm, "end": v(-10.32, -3.7) * mm});
            skLineSegment(sketch, "E365", {"start": v(-10.32, -3.7) * mm, "end": v(-10.27, 1.11) * mm});
            skLineSegment(sketch, "E366", {"start": v(0.8, 1.2) * mm, "end": v(0.8, 6.09) * mm});
            skLineSegment(sketch, "E367", {"start": v(0.8, 6.09) * mm, "end": v(1.83, 6.09) * mm});
            skLineSegment(sketch, "E368", {"start": v(1.83, 6.09) * mm, "end": v(2.06, 6.09) * mm});
            skLineSegment(sketch, "E369", {"start": v(2.06, 6.09) * mm, "end": v(2.75, 5.94) * mm});
            skLineSegment(sketch, "E370", {"start": v(2.75, 5.94) * mm, "end": v(3.43, 5.62) * mm});
            skLineSegment(sketch, "E371", {"start": v(3.43, 5.62) * mm, "end": v(3.55, 5.53) * mm});
            skLineSegment(sketch, "E372", {"start": v(3.55, 5.53) * mm, "end": v(3.64, 5.45) * mm});
            skLineSegment(sketch, "E373", {"start": v(3.64, 5.45) * mm, "end": v(3.9, 5.2) * mm});
            skLineSegment(sketch, "E374", {"start": v(3.9, 5.2) * mm, "end": v(4.12, 4.8) * mm});
            skLineSegment(sketch, "E375", {"start": v(4.12, 4.8) * mm, "end": v(4.21, 4.22) * mm});
            skLineSegment(sketch, "E376", {"start": v(4.21, 4.22) * mm, "end": v(4.23, 3.54) * mm});
            skLineSegment(sketch, "E377", {"start": v(4.23, 3.54) * mm, "end": v(4.23, 3.3) * mm});
            skLineSegment(sketch, "E378", {"start": v(4.23, 3.3) * mm, "end": v(4.23, 3.08) * mm});
            skLineSegment(sketch, "E379", {"start": v(4.23, 3.08) * mm, "end": v(4.21, 2.4) * mm});
            skLineSegment(sketch, "E380", {"start": v(4.21, 2.4) * mm, "end": v(4.12, 1.8) * mm});
            skLineSegment(sketch, "E381", {"start": v(4.12, 1.8) * mm, "end": v(3.9, 1.42) * mm});
            skLineSegment(sketch, "E382", {"start": v(3.9, 1.42) * mm, "end": v(3.64, 1.16) * mm});
            skLineSegment(sketch, "E383", {"start": v(3.64, 1.16) * mm, "end": v(3.55, 1.08) * mm});
            skLineSegment(sketch, "E384", {"start": v(3.55, 1.08) * mm, "end": v(3.45, 1) * mm});
            skLineSegment(sketch, "E385", {"start": v(3.45, 1) * mm, "end": v(2.82, 0.69) * mm});
            skLineSegment(sketch, "E386", {"start": v(2.82, 0.69) * mm, "end": v(2.27, 0.53) * mm});
            skLineSegment(sketch, "E387", {"start": v(2.27, 0.53) * mm, "end": v(2.1, 0.53) * mm});
            skLineSegment(sketch, "E388", {"start": v(2.1, 0.53) * mm, "end": v(1.32, 0.53) * mm});
            skLineSegment(sketch, "E389", {"start": v(1.32, 0.53) * mm, "end": v(1.32, -1.59) * mm});
            skLineSegment(sketch, "E390", {"start": v(1.32, -1.59) * mm, "end": v(1.32, -1.8) * mm});
            skLineSegment(sketch, "E391", {"start": v(1.32, -1.8) * mm, "end": v(1.3, -2.44) * mm});
            skLineSegment(sketch, "E392", {"start": v(1.3, -2.44) * mm, "end": v(1.25, -3.11) * mm});
            skLineSegment(sketch, "E393", {"start": v(1.25, -3.11) * mm, "end": v(1.17, -3.55) * mm});
            skLineSegment(sketch, "E394", {"start": v(1.17, -3.55) * mm, "end": v(1.08, -3.7) * mm});
            skLineSegment(sketch, "E395", {"start": v(1.08, -3.7) * mm, "end": v(1.06, -3.7) * mm});
            skLineSegment(sketch, "E396", {"start": v(1.06, -3.7) * mm, "end": v(1.03, -3.7) * mm});
            skLineSegment(sketch, "E397", {"start": v(1.03, -3.7) * mm, "end": v(0.95, -3.37) * mm});
            skLineSegment(sketch, "E398", {"start": v(0.95, -3.37) * mm, "end": v(0.87, -2.42) * mm});
            skLineSegment(sketch, "E399", {"start": v(0.87, -2.42) * mm, "end": v(0.81, -0.88) * mm});
            skLineSegment(sketch, "E400", {"start": v(0.81, -0.88) * mm, "end": v(0.8, 0.67) * mm});
            skLineSegment(sketch, "E401", {"start": v(0.8, 0.67) * mm, "end": v(0.8, 1.2) * mm});
            skLineSegment(sketch, "E402", {"start": v(3.44, 1.83) * mm, "end": v(3.52, 2) * mm});
            skLineSegment(sketch, "E403", {"start": v(3.52, 2) * mm, "end": v(3.65, 2.57) * mm});
            skLineSegment(sketch, "E404", {"start": v(3.65, 2.57) * mm, "end": v(3.69, 3.47) * mm});
            skLineSegment(sketch, "E405", {"start": v(3.69, 3.47) * mm, "end": v(3.56, 4.3) * mm});
            skLineSegment(sketch, "E406", {"start": v(3.56, 4.3) * mm, "end": v(3.39, 4.76) * mm});
            skLineSegment(sketch, "E407", {"start": v(3.39, 4.76) * mm, "end": v(3.28, 4.87) * mm});
            skLineSegment(sketch, "E408", {"start": v(3.28, 4.87) * mm, "end": v(3.23, 4.93) * mm});
            skLineSegment(sketch, "E409", {"start": v(3.23, 4.93) * mm, "end": v(2.76, 5.17) * mm});
            skLineSegment(sketch, "E410", {"start": v(2.76, 5.17) * mm, "end": v(2.26, 5.3) * mm});
            skLineSegment(sketch, "E411", {"start": v(2.26, 5.3) * mm, "end": v(2.1, 5.3) * mm});
            skLineSegment(sketch, "E412", {"start": v(2.1, 5.3) * mm, "end": v(1.32, 5.3) * mm});
            skLineSegment(sketch, "E413", {"start": v(1.32, 5.3) * mm, "end": v(1.32, 1.32) * mm});
            skLineSegment(sketch, "E414", {"start": v(1.32, 1.32) * mm, "end": v(2.25, 1.32) * mm});
            skLineSegment(sketch, "E415", {"start": v(2.25, 1.32) * mm, "end": v(2.44, 1.32) * mm});
            skLineSegment(sketch, "E416", {"start": v(2.44, 1.32) * mm, "end": v(3, 1.45) * mm});
            skLineSegment(sketch, "E417", {"start": v(3, 1.45) * mm, "end": v(3.39, 1.74) * mm});
            skLineSegment(sketch, "E418", {"start": v(3.39, 1.74) * mm, "end": v(3.44, 1.83) * mm});
            skLineSegment(sketch, "E419", {"start": v(6, -3.23) * mm, "end": v(5.93, -3.14) * mm});
            skLineSegment(sketch, "E420", {"start": v(5.93, -3.14) * mm, "end": v(5.78, -2.82) * mm});
            skLineSegment(sketch, "E421", {"start": v(5.78, -2.82) * mm, "end": v(5.64, -2.08) * mm});
            skLineSegment(sketch, "E422", {"start": v(5.64, -2.08) * mm, "end": v(5.57, -0.8) * mm});
            skLineSegment(sketch, "E423", {"start": v(5.57, -0.8) * mm, "end": v(5.56, 0.73) * mm});
            skLineSegment(sketch, "E424", {"start": v(5.56, 0.73) * mm, "end": v(5.56, 1.24) * mm});
            skLineSegment(sketch, "E425", {"start": v(5.56, 1.24) * mm, "end": v(5.56, 1.61) * mm});
            skLineSegment(sketch, "E426", {"start": v(5.56, 1.61) * mm, "end": v(5.57, 2.72) * mm});
            skLineSegment(sketch, "E427", {"start": v(5.57, 2.72) * mm, "end": v(5.6, 3.87) * mm});
            skLineSegment(sketch, "E428", {"start": v(5.6, 3.87) * mm, "end": v(5.7, 4.72) * mm});
            skLineSegment(sketch, "E429", {"start": v(5.7, 4.72) * mm, "end": v(5.84, 5.32) * mm});
            skLineSegment(sketch, "E430", {"start": v(5.84, 5.32) * mm, "end": v(6.06, 5.72) * mm});
            skLineSegment(sketch, "E431", {"start": v(6.06, 5.72) * mm, "end": v(6.37, 5.95) * mm});
            skLineSegment(sketch, "E432", {"start": v(6.37, 5.95) * mm, "end": v(6.79, 6.06) * mm});
            skLineSegment(sketch, "E433", {"start": v(6.79, 6.06) * mm, "end": v(7.2, 6.09) * mm});
            skLineSegment(sketch, "E434", {"start": v(7.2, 6.09) * mm, "end": v(7.33, 6.09) * mm});
            skLineSegment(sketch, "E435", {"start": v(7.33, 6.09) * mm, "end": v(7.45, 6.09) * mm});
            skLineSegment(sketch, "E436", {"start": v(7.45, 6.09) * mm, "end": v(7.82, 6.06) * mm});
            skLineSegment(sketch, "E437", {"start": v(7.82, 6.06) * mm, "end": v(8.21, 5.94) * mm});
            skLineSegment(sketch, "E438", {"start": v(8.21, 5.94) * mm, "end": v(8.5, 5.7) * mm});
            skLineSegment(sketch, "E439", {"start": v(8.5, 5.7) * mm, "end": v(8.72, 5.28) * mm});
            skLineSegment(sketch, "E440", {"start": v(8.72, 5.28) * mm, "end": v(8.86, 4.66) * mm});
            skLineSegment(sketch, "E441", {"start": v(8.86, 4.66) * mm, "end": v(8.94, 3.79) * mm});
            skLineSegment(sketch, "E442", {"start": v(8.94, 3.79) * mm, "end": v(8.98, 2.63) * mm});
            skLineSegment(sketch, "E443", {"start": v(8.98, 2.63) * mm, "end": v(9, 1.51) * mm});
            skLineSegment(sketch, "E444", {"start": v(9, 1.51) * mm, "end": v(9, 1.14) * mm});
            skLineSegment(sketch, "E445", {"start": v(9, 1.14) * mm, "end": v(9, 0.6) * mm});
            skLineSegment(sketch, "E446", {"start": v(9, 0.6) * mm, "end": v(8.98, -0.98) * mm});
            skLineSegment(sketch, "E447", {"start": v(8.98, -0.98) * mm, "end": v(8.92, -2.24) * mm});
            skLineSegment(sketch, "E448", {"start": v(8.92, -2.24) * mm, "end": v(8.77, -2.9) * mm});
            skLineSegment(sketch, "E449", {"start": v(8.77, -2.9) * mm, "end": v(8.6, -3.19) * mm});
            skLineSegment(sketch, "E450", {"start": v(8.6, -3.19) * mm, "end": v(8.52, -3.25) * mm});
            skLineSegment(sketch, "E451", {"start": v(8.52, -3.25) * mm, "end": v(8.4, -3.36) * mm});
            skLineSegment(sketch, "E452", {"start": v(8.4, -3.36) * mm, "end": v(7.92, -3.58) * mm});
            skLineSegment(sketch, "E453", {"start": v(7.92, -3.58) * mm, "end": v(7.21, -3.68) * mm});
            skLineSegment(sketch, "E454", {"start": v(7.21, -3.68) * mm, "end": v(6.53, -3.56) * mm});
            skLineSegment(sketch, "E455", {"start": v(6.53, -3.56) * mm, "end": v(6.1, -3.34) * mm});
            skLineSegment(sketch, "E456", {"start": v(6.1, -3.34) * mm, "end": v(6, -3.23) * mm});
            skLineSegment(sketch, "E457", {"start": v(8.4, -2.37) * mm, "end": v(8.37, -2.16) * mm});
            skLineSegment(sketch, "E458", {"start": v(8.37, -2.16) * mm, "end": v(8.28, -1.5) * mm});
            skLineSegment(sketch, "E459", {"start": v(8.28, -1.5) * mm, "end": v(8.22, -0.42) * mm});
            skLineSegment(sketch, "E460", {"start": v(8.22, -0.42) * mm, "end": v(8.2, 0.7) * mm});
            skLineSegment(sketch, "E461", {"start": v(8.2, 0.7) * mm, "end": v(8.2, 1.08) * mm});
            skLineSegment(sketch, "E462", {"start": v(8.2, 1.08) * mm, "end": v(8.2, 1.64) * mm});
            skLineSegment(sketch, "E463", {"start": v(8.2, 1.64) * mm, "end": v(8.16, 3.3) * mm});
            skLineSegment(sketch, "E464", {"start": v(8.16, 3.3) * mm, "end": v(7.99, 4.67) * mm});
            skLineSegment(sketch, "E465", {"start": v(7.99, 4.67) * mm, "end": v(7.67, 5.36) * mm});
            skLineSegment(sketch, "E466", {"start": v(7.67, 5.36) * mm, "end": v(7.27, 5.56) * mm});
            skLineSegment(sketch, "E467", {"start": v(7.27, 5.56) * mm, "end": v(7.14, 5.56) * mm});
            skLineSegment(sketch, "E468", {"start": v(7.14, 5.56) * mm, "end": v(7.09, 5.56) * mm});
            skLineSegment(sketch, "E469", {"start": v(7.09, 5.56) * mm, "end": v(6.91, 5.53) * mm});
            skLineSegment(sketch, "E470", {"start": v(6.91, 5.53) * mm, "end": v(6.73, 5.41) * mm});
            skLineSegment(sketch, "E471", {"start": v(6.73, 5.41) * mm, "end": v(6.6, 5.18) * mm});
            skLineSegment(sketch, "E472", {"start": v(6.6, 5.18) * mm, "end": v(6.5, 4.77) * mm});
            skLineSegment(sketch, "E473", {"start": v(6.5, 4.77) * mm, "end": v(6.42, 4.17) * mm});
            skLineSegment(sketch, "E474", {"start": v(6.42, 4.17) * mm, "end": v(6.37, 3.31) * mm});
            skLineSegment(sketch, "E475", {"start": v(6.37, 3.31) * mm, "end": v(6.33, 2.18) * mm});
            skLineSegment(sketch, "E476", {"start": v(6.33, 2.18) * mm, "end": v(6.3, 1.08) * mm});
            skLineSegment(sketch, "E477", {"start": v(6.3, 1.08) * mm, "end": v(6.3, 0.71) * mm});
            skLineSegment(sketch, "E478", {"start": v(6.3, 0.71) * mm, "end": v(6.29, 0.28) * mm});
            skLineSegment(sketch, "E479", {"start": v(6.29, 0.28) * mm, "end": v(6.28, -1.01) * mm});
            skLineSegment(sketch, "E480", {"start": v(6.28, -1.01) * mm, "end": v(6.3, -2.13) * mm});
            skLineSegment(sketch, "E481", {"start": v(6.3, -2.13) * mm, "end": v(6.4, -2.73) * mm});
            skLineSegment(sketch, "E482", {"start": v(6.4, -2.73) * mm, "end": v(6.52, -2.91) * mm});
            skLineSegment(sketch, "E483", {"start": v(6.52, -2.91) * mm, "end": v(6.56, -2.91) * mm});
            skLineSegment(sketch, "E484", {"start": v(6.56, -2.91) * mm, "end": v(6.62, -2.91) * mm});
            skLineSegment(sketch, "E485", {"start": v(6.62, -2.91) * mm, "end": v(6.78, -2.98) * mm});
            skLineSegment(sketch, "E486", {"start": v(6.78, -2.98) * mm, "end": v(6.88, -3.1) * mm});
            skLineSegment(sketch, "E487", {"start": v(6.88, -3.1) * mm, "end": v(6.88, -3.15) * mm});
            skLineSegment(sketch, "E488", {"start": v(6.88, -3.15) * mm, "end": v(6.88, -3.17) * mm});
            skLineSegment(sketch, "E489", {"start": v(6.88, -3.17) * mm, "end": v(7.12, -3.25) * mm});
            skLineSegment(sketch, "E490", {"start": v(7.12, -3.25) * mm, "end": v(7.66, -3.14) * mm});
            skLineSegment(sketch, "E491", {"start": v(7.66, -3.14) * mm, "end": v(8.25, -2.9) * mm});
            skLineSegment(sketch, "E492", {"start": v(8.25, -2.9) * mm, "end": v(8.35, -2.73) * mm});
            skLineSegment(sketch, "E493", {"start": v(8.35, -2.73) * mm, "end": v(8.38, -2.56) * mm});
            skLineSegment(sketch, "E494", {"start": v(11.5, 0.71) * mm, "end": v(11.5, 1.08) * mm});
            skLineSegment(sketch, "E495", {"start": v(11.5, 1.08) * mm, "end": v(11.5, 2.17) * mm});
            skLineSegment(sketch, "E496", {"start": v(11.5, 2.17) * mm, "end": v(11.5, 3.26) * mm});
            skLineSegment(sketch, "E497", {"start": v(11.5, 3.26) * mm, "end": v(11.48, 4.05) * mm});
            skLineSegment(sketch, "E498", {"start": v(11.48, 4.05) * mm, "end": v(11.43, 4.6) * mm});
            skLineSegment(sketch, "E499", {"start": v(11.43, 4.6) * mm, "end": v(11.36, 4.93) * mm});
            skLineSegment(sketch, "E500", {"start": v(11.36, 4.93) * mm, "end": v(11.25, 5.13) * mm});
            skLineSegment(sketch, "E501", {"start": v(11.25, 5.13) * mm, "end": v(11.1, 5.23) * mm});
            skLineSegment(sketch, "E502", {"start": v(11.1, 5.23) * mm, "end": v(10.95, 5.28) * mm});
            skLineSegment(sketch, "E503", {"start": v(10.95, 5.28) * mm, "end": v(10.9, 5.3) * mm});
            skLineSegment(sketch, "E504", {"start": v(10.9, 5.3) * mm, "end": v(10.75, 5.33) * mm});
            skLineSegment(sketch, "E505", {"start": v(10.75, 5.33) * mm, "end": v(10.32, 5.5) * mm});
            skLineSegment(sketch, "E506", {"start": v(10.32, 5.5) * mm, "end": v(10.31, 5.73) * mm});
            skLineSegment(sketch, "E507", {"start": v(10.31, 5.73) * mm, "end": v(10.84, 5.92) * mm});
            skLineSegment(sketch, "E508", {"start": v(10.84, 5.92) * mm, "end": v(11.6, 6.02) * mm});
            skLineSegment(sketch, "E509", {"start": v(11.6, 6.02) * mm, "end": v(11.85, 6.03) * mm});
            skLineSegment(sketch, "E510", {"start": v(11.85, 6.03) * mm, "end": v(12.06, 6.04) * mm});
            skLineSegment(sketch, "E511", {"start": v(12.06, 6.04) * mm, "end": v(12.68, 6.05) * mm});
            skLineSegment(sketch, "E512", {"start": v(12.68, 6.05) * mm, "end": v(13.18, 6) * mm});
            skLineSegment(sketch, "E513", {"start": v(13.18, 6) * mm, "end": v(13.43, 5.9) * mm});
            skLineSegment(sketch, "E514", {"start": v(13.43, 5.9) * mm, "end": v(13.5, 5.74) * mm});
            skLineSegment(sketch, "E515", {"start": v(13.5, 5.74) * mm, "end": v(13.5, 5.69) * mm});
            skLineSegment(sketch, "E516", {"start": v(13.5, 5.69) * mm, "end": v(13.5, 5.62) * mm});
            skLineSegment(sketch, "E517", {"start": v(13.5, 5.62) * mm, "end": v(13.32, 5.4) * mm});
            skLineSegment(sketch, "E518", {"start": v(13.32, 5.4) * mm, "end": v(12.95, 5.3) * mm});
            skLineSegment(sketch, "E519", {"start": v(12.95, 5.3) * mm, "end": v(12.83, 5.3) * mm});
            skLineSegment(sketch, "E520", {"start": v(12.83, 5.3) * mm, "end": v(12.17, 5.3) * mm});
            skLineSegment(sketch, "E521", {"start": v(12.17, 5.3) * mm, "end": v(12.17, 0.8) * mm});
            skLineSegment(sketch, "E522", {"start": v(12.17, 0.8) * mm, "end": v(12.17, 0.26) * mm});
            skLineSegment(sketch, "E523", {"start": v(12.17, 0.26) * mm, "end": v(12.15, -1.35) * mm});
            skLineSegment(sketch, "E524", {"start": v(12.15, -1.35) * mm, "end": v(12.1, -2.73) * mm});
            skLineSegment(sketch, "E525", {"start": v(12.1, -2.73) * mm, "end": v(12, -3.48) * mm});
            skLineSegment(sketch, "E526", {"start": v(12, -3.48) * mm, "end": v(11.9, -3.7) * mm});
            skLineSegment(sketch, "E527", {"start": v(11.9, -3.7) * mm, "end": v(11.85, -3.7) * mm});
            skLineSegment(sketch, "E528", {"start": v(11.85, -3.7) * mm, "end": v(11.81, -3.7) * mm});
            skLineSegment(sketch, "E529", {"start": v(11.81, -3.7) * mm, "end": v(11.69, -3.49) * mm});
            skLineSegment(sketch, "E530", {"start": v(11.69, -3.49) * mm, "end": v(11.58, -2.75) * mm});
            skLineSegment(sketch, "E531", {"start": v(11.58, -2.75) * mm, "end": v(11.53, -1.4) * mm});
            skLineSegment(sketch, "E532", {"start": v(11.53, -1.4) * mm, "end": v(11.5, 0.19) * mm});
            skLineSegment(sketch, "E533", {"start": v(11.5, 0.19) * mm, "end": v(11.5, 0.71) * mm});
            skLineSegment(sketch, "E534", {"start": v(14.6, 5.3) * mm, "end": v(14.6, 5.4) * mm});
            skLineSegment(sketch, "E535", {"start": v(14.6, 5.4) * mm, "end": v(14.64, 5.85) * mm});
            skLineSegment(sketch, "E536", {"start": v(14.64, 5.85) * mm, "end": v(14.77, 6.09) * mm});
            skLineSegment(sketch, "E537", {"start": v(14.77, 6.09) * mm, "end": v(14.82, 6.09) * mm});
            skLineSegment(sketch, "E538", {"start": v(14.82, 6.09) * mm, "end": v(14.86, 6.09) * mm});
            skLineSegment(sketch, "E539", {"start": v(14.86, 6.09) * mm, "end": v(15, 5.85) * mm});
            skLineSegment(sketch, "E540", {"start": v(15, 5.85) * mm, "end": v(15.08, 5.43) * mm});
            skLineSegment(sketch, "E541", {"start": v(15.08, 5.43) * mm, "end": v(15.08, 5.3) * mm});
            skLineSegment(sketch, "E542", {"start": v(15.08, 5.3) * mm, "end": v(15.08, 5.15) * mm});
            skLineSegment(sketch, "E543", {"start": v(15.08, 5.15) * mm, "end": v(15.01, 4.73) * mm});
            skLineSegment(sketch, "E544", {"start": v(15.01, 4.73) * mm, "end": v(14.9, 4.5) * mm});
            skLineSegment(sketch, "E545", {"start": v(14.9, 4.5) * mm, "end": v(14.87, 4.5) * mm});
            skLineSegment(sketch, "E546", {"start": v(14.87, 4.5) * mm, "end": v(14.83, 4.5) * mm});
            skLineSegment(sketch, "E547", {"start": v(14.83, 4.5) * mm, "end": v(14.7, 4.73) * mm});
            skLineSegment(sketch, "E548", {"start": v(14.7, 4.73) * mm, "end": v(14.61, 5.18) * mm});
            skLineSegment(sketch, "E549", {"start": v(14.61, 5.18) * mm, "end": v(14.6, 5.3) * mm});
            skLineSegment(sketch, "E550", {"start": v(-23.55, 0) * mm, "end": v(-23.55, 23.55) * mm});
            skLineSegment(sketch, "E551", {"start": v(-23.55, 23.55) * mm, "end": v(23.55, 23.55) * mm});
            skLineSegment(sketch, "E552", {"start": v(23.55, 23.55) * mm, "end": v(23.55, -23.55) * mm});
            skLineSegment(sketch, "E553", {"start": v(23.55, -23.55) * mm, "end": v(-23.55, -23.55) * mm});
            skLineSegment(sketch, "E554", {"start": v(-23.55, -23.55) * mm, "end": v(-23.55, 0) * mm});
            skLineSegment(sketch, "E555", {"start": v(2.28, -21.43) * mm, "end": v(3.04, -21.33) * mm});
            skLineSegment(sketch, "E556", {"start": v(3.04, -21.33) * mm, "end": v(6.18, -20.67) * mm});
            skLineSegment(sketch, "E557", {"start": v(6.18, -20.67) * mm, "end": v(8.99, -19.61) * mm});
            skLineSegment(sketch, "E558", {"start": v(8.99, -19.61) * mm, "end": v(9.58, -19.31) * mm});
            skLineSegment(sketch, "E559", {"start": v(9.58, -19.31) * mm, "end": v(10.29, -18.96) * mm});
            skLineSegment(sketch, "E560", {"start": v(10.29, -18.96) * mm, "end": v(12.32, -17.7) * mm});
            skLineSegment(sketch, "E561", {"start": v(12.32, -17.7) * mm, "end": v(14.7, -15.8) * mm});
            skLineSegment(sketch, "E562", {"start": v(14.7, -15.8) * mm, "end": v(16.77, -13.55) * mm});
            skLineSegment(sketch, "E563", {"start": v(16.77, -13.55) * mm, "end": v(18.15, -11.6) * mm});
            skLineSegment(sketch, "E564", {"start": v(18.15, -11.6) * mm, "end": v(18.55, -10.93) * mm});
            skLineSegment(sketch, "E565", {"start": v(18.55, -10.93) * mm, "end": v(18.92, -10.28) * mm});
            skLineSegment(sketch, "E566", {"start": v(18.92, -10.28) * mm, "end": v(19.92, -8.25) * mm});
            skLineSegment(sketch, "E567", {"start": v(19.92, -8.25) * mm, "end": v(20.84, -5.63) * mm});
            skLineSegment(sketch, "E568", {"start": v(20.84, -5.63) * mm, "end": v(21.36, -2.9) * mm});
            skLineSegment(sketch, "E569", {"start": v(21.36, -2.9) * mm, "end": v(21.52, -0.62) * mm});
            skLineSegment(sketch, "E570", {"start": v(21.52, -0.62) * mm, "end": v(21.51, 0.13) * mm});
            skLineSegment(sketch, "E571", {"start": v(21.51, 0.13) * mm, "end": v(21.51, 1.02) * mm});
            skLineSegment(sketch, "E572", {"start": v(21.51, 1.02) * mm, "end": v(21.24, 3.66) * mm});
            skLineSegment(sketch, "E573", {"start": v(21.24, 3.66) * mm, "end": v(20.4, 7) * mm});
            skLineSegment(sketch, "E574", {"start": v(20.4, 7) * mm, "end": v(19, 10.17) * mm});
            skLineSegment(sketch, "E575", {"start": v(19, 10.17) * mm, "end": v(17.56, 12.52) * mm});
            skLineSegment(sketch, "E576", {"start": v(17.56, 12.52) * mm, "end": v(17.01, 13.26) * mm});
            skLineSegment(sketch, "E577", {"start": v(17.01, 13.26) * mm, "end": v(16.82, 13.5) * mm});
            skLineSegment(sketch, "E578", {"start": v(16.82, 13.5) * mm, "end": v(16.28, 14.27) * mm});
            skLineSegment(sketch, "E579", {"start": v(16.28, 14.27) * mm, "end": v(15.85, 15) * mm});
            skLineSegment(sketch, "E580", {"start": v(15.85, 15) * mm, "end": v(15.66, 15.63) * mm});
            skLineSegment(sketch, "E581", {"start": v(15.66, 15.63) * mm, "end": v(15.61, 16.15) * mm});
            skLineSegment(sketch, "E582", {"start": v(15.61, 16.15) * mm, "end": v(15.61, 16.32) * mm});
            skLineSegment(sketch, "E583", {"start": v(15.61, 16.32) * mm, "end": v(15.61, 16.65) * mm});
            skLineSegment(sketch, "E584", {"start": v(15.61, 16.65) * mm, "end": v(15.51, 17.62) * mm});
            skLineSegment(sketch, "E585", {"start": v(15.51, 17.62) * mm, "end": v(15.2, 18.77) * mm});
            skLineSegment(sketch, "E586", {"start": v(15.2, 18.77) * mm, "end": v(14.66, 19.81) * mm});
            skLineSegment(sketch, "E587", {"start": v(14.66, 19.81) * mm, "end": v(14.08, 20.57) * mm});
            skLineSegment(sketch, "E588", {"start": v(14.08, 20.57) * mm, "end": v(13.86, 20.8) * mm});
            skLineSegment(sketch, "E589", {"start": v(13.86, 20.8) * mm, "end": v(13.75, 20.91) * mm});
            skLineSegment(sketch, "E590", {"start": v(13.75, 20.91) * mm, "end": v(13.4, 21.25) * mm});
            skLineSegment(sketch, "E591", {"start": v(13.4, 21.25) * mm, "end": v(13, 21.62) * mm});
            skLineSegment(sketch, "E592", {"start": v(13, 21.62) * mm, "end": v(12.67, 21.87) * mm});
            skLineSegment(sketch, "E593", {"start": v(12.67, 21.87) * mm, "end": v(12.53, 21.96) * mm});
            skLineSegment(sketch, "E594", {"start": v(12.53, 21.96) * mm, "end": v(12.49, 21.96) * mm});
            skLineSegment(sketch, "E595", {"start": v(12.49, 21.96) * mm, "end": v(12.43, 21.96) * mm});
            skLineSegment(sketch, "E596", {"start": v(12.43, 21.96) * mm, "end": v(12.26, 22.05) * mm});
            skLineSegment(sketch, "E597", {"start": v(12.26, 22.05) * mm, "end": v(12.13, 22.21) * mm});
            skLineSegment(sketch, "E598", {"start": v(12.13, 22.21) * mm, "end": v(12.12, 22.25) * mm});
            skLineSegment(sketch, "E599", {"start": v(12.12, 22.25) * mm, "end": v(12.1, 22.28) * mm});
            skLineSegment(sketch, "E600", {"start": v(12.1, 22.28) * mm, "end": v(11.9, 22.47) * mm});
            skLineSegment(sketch, "E601", {"start": v(11.9, 22.47) * mm, "end": v(11.58, 22.6) * mm});
            skLineSegment(sketch, "E602", {"start": v(11.58, 22.6) * mm, "end": v(11.5, 22.62) * mm});
            skLineSegment(sketch, "E603", {"start": v(11.5, 22.62) * mm, "end": v(11.44, 22.64) * mm});
            skLineSegment(sketch, "E604", {"start": v(11.44, 22.64) * mm, "end": v(11.13, 22.7) * mm});
            skLineSegment(sketch, "E605", {"start": v(11.13, 22.7) * mm, "end": v(10.98, 22.74) * mm});
            skLineSegment(sketch, "E606", {"start": v(10.98, 22.74) * mm, "end": v(10.98, 22.75) * mm});
            skLineSegment(sketch, "E607", {"start": v(10.98, 22.75) * mm, "end": v(10.98, 22.78) * mm});
            skLineSegment(sketch, "E608", {"start": v(10.98, 22.78) * mm, "end": v(10.77, 22.86) * mm});
            skLineSegment(sketch, "E609", {"start": v(10.77, 22.86) * mm, "end": v(10.26, 22.95) * mm});
            skLineSegment(sketch, "E610", {"start": v(10.26, 22.95) * mm, "end": v(9.57, 23.02) * mm});
            skLineSegment(sketch, "E611", {"start": v(9.57, 23.02) * mm, "end": v(9.04, 23.04) * mm});
            skLineSegment(sketch, "E612", {"start": v(9.04, 23.04) * mm, "end": v(8.86, 23.04) * mm});
            skLineSegment(sketch, "E613", {"start": v(8.86, 23.04) * mm, "end": v(8.69, 23.04) * mm});
            skLineSegment(sketch, "E614", {"start": v(8.69, 23.04) * mm, "end": v(8.15, 23.02) * mm});
            skLineSegment(sketch, "E615", {"start": v(8.15, 23.02) * mm, "end": v(7.47, 22.95) * mm});
            skLineSegment(sketch, "E616", {"start": v(7.47, 22.95) * mm, "end": v(6.95, 22.86) * mm});
            skLineSegment(sketch, "E617", {"start": v(6.95, 22.86) * mm, "end": v(6.75, 22.78) * mm});
            skLineSegment(sketch, "E618", {"start": v(6.75, 22.78) * mm, "end": v(6.75, 22.75) * mm});
            skLineSegment(sketch, "E619", {"start": v(6.75, 22.75) * mm, "end": v(6.75, 22.74) * mm});
            skLineSegment(sketch, "E620", {"start": v(6.75, 22.74) * mm, "end": v(6.6, 22.7) * mm});
            skLineSegment(sketch, "E621", {"start": v(6.6, 22.7) * mm, "end": v(6.34, 22.64) * mm});
            skLineSegment(sketch, "E622", {"start": v(6.34, 22.64) * mm, "end": v(6.27, 22.62) * mm});
            skLineSegment(sketch, "E623", {"start": v(6.27, 22.62) * mm, "end": v(6.2, 22.6) * mm});
            skLineSegment(sketch, "E624", {"start": v(6.2, 22.6) * mm, "end": v(5.69, 22.37) * mm});
            skLineSegment(sketch, "E625", {"start": v(5.69, 22.37) * mm, "end": v(5.07, 21.97) * mm});
            skLineSegment(sketch, "E626", {"start": v(5.07, 21.97) * mm, "end": v(4.95, 21.88) * mm});
            skLineSegment(sketch, "E627", {"start": v(4.95, 21.88) * mm, "end": v(4.82, 21.79) * mm});
            skLineSegment(sketch, "E628", {"start": v(4.82, 21.79) * mm, "end": v(4.43, 21.53) * mm});
            skLineSegment(sketch, "E629", {"start": v(4.43, 21.53) * mm, "end": v(3.94, 21.37) * mm});
            skLineSegment(sketch, "E630", {"start": v(3.94, 21.37) * mm, "end": v(3.24, 21.36) * mm});
            skLineSegment(sketch, "E631", {"start": v(3.24, 21.36) * mm, "end": v(2.4, 21.45) * mm});
            skLineSegment(sketch, "E632", {"start": v(2.4, 21.45) * mm, "end": v(2.12, 21.48) * mm});
            skLineSegment(sketch, "E633", {"start": v(2.12, 21.48) * mm, "end": v(1.36, 21.58) * mm});
            skLineSegment(sketch, "E634", {"start": v(1.36, 21.58) * mm, "end": v(-0.95, 21.56) * mm});
            skLineSegment(sketch, "E635", {"start": v(-0.95, 21.56) * mm, "end": v(-4.24, 21.13) * mm});
            skLineSegment(sketch, "E636", {"start": v(-4.24, 21.13) * mm, "end": v(-7.46, 20.26) * mm});
            skLineSegment(sketch, "E637", {"start": v(-7.46, 20.26) * mm, "end": v(-9.64, 19.38) * mm});
            skLineSegment(sketch, "E638", {"start": v(-9.64, 19.38) * mm, "end": v(-10.32, 19) * mm});
            skLineSegment(sketch, "E639", {"start": v(-10.32, 19) * mm, "end": v(-10.46, 18.92) * mm});
            skLineSegment(sketch, "E640", {"start": v(-10.46, 18.92) * mm, "end": v(-10.9, 18.67) * mm});
            skLineSegment(sketch, "E641", {"start": v(-10.9, 18.67) * mm, "end": v(-11.38, 18.38) * mm});
            skLineSegment(sketch, "E642", {"start": v(-11.38, 18.38) * mm, "end": v(-11.74, 18.15) * mm});
            skLineSegment(sketch, "E643", {"start": v(-11.74, 18.15) * mm, "end": v(-11.89, 18.05) * mm});
            skLineSegment(sketch, "E644", {"start": v(-11.89, 18.05) * mm, "end": v(-11.9, 18.02) * mm});
            skLineSegment(sketch, "E645", {"start": v(-11.9, 18.02) * mm, "end": v(-11.93, 18) * mm});
            skLineSegment(sketch, "E646", {"start": v(-11.93, 18) * mm, "end": v(-12.22, 17.8) * mm});
            skLineSegment(sketch, "E647", {"start": v(-12.22, 17.8) * mm, "end": v(-12.68, 17.52) * mm});
            skLineSegment(sketch, "E648", {"start": v(-12.68, 17.52) * mm, "end": v(-12.78, 17.46) * mm});
            skLineSegment(sketch, "E649", {"start": v(-12.78, 17.46) * mm, "end": v(-12.98, 17.36) * mm});
            skLineSegment(sketch, "E650", {"start": v(-12.98, 17.36) * mm, "end": v(-13.52, 16.95) * mm});
            skLineSegment(sketch, "E651", {"start": v(-13.52, 16.95) * mm, "end": v(-14.43, 16.13) * mm});
            skLineSegment(sketch, "E652", {"start": v(-14.43, 16.13) * mm, "end": v(-15.42, 15.1) * mm});
            skLineSegment(sketch, "E653", {"start": v(-15.42, 15.1) * mm, "end": v(-16.42, 13.97) * mm});
            skLineSegment(sketch, "E654", {"start": v(-16.42, 13.97) * mm, "end": v(-17.33, 12.83) * mm});
            skLineSegment(sketch, "E655", {"start": v(-17.33, 12.83) * mm, "end": v(-18.09, 11.76) * mm});
            skLineSegment(sketch, "E656", {"start": v(-18.09, 11.76) * mm, "end": v(-18.6, 10.87) * mm});
            skLineSegment(sketch, "E657", {"start": v(-18.6, 10.87) * mm, "end": v(-18.79, 10.42) * mm});
            skLineSegment(sketch, "E658", {"start": v(-18.79, 10.42) * mm, "end": v(-18.79, 10.27) * mm});
            skLineSegment(sketch, "E659", {"start": v(-18.79, 10.27) * mm, "end": v(-18.79, 10.18) * mm});
            skLineSegment(sketch, "E660", {"start": v(-18.79, 10.18) * mm, "end": v(-18.86, 9.93) * mm});
            skLineSegment(sketch, "E661", {"start": v(-18.86, 9.93) * mm, "end": v(-19, 9.79) * mm});
            skLineSegment(sketch, "E662", {"start": v(-19, 9.79) * mm, "end": v(-19.05, 9.79) * mm});
            skLineSegment(sketch, "E663", {"start": v(-19.05, 9.79) * mm, "end": v(-19.14, 9.79) * mm});
            skLineSegment(sketch, "E664", {"start": v(-19.14, 9.79) * mm, "end": v(-19.4, 9.41) * mm});
            skLineSegment(sketch, "E665", {"start": v(-19.4, 9.41) * mm, "end": v(-19.9, 8.4) * mm});
            skLineSegment(sketch, "E666", {"start": v(-19.9, 8.4) * mm, "end": v(-20.44, 6.97) * mm});
            skLineSegment(sketch, "E667", {"start": v(-20.44, 6.97) * mm, "end": v(-20.84, 5.71) * mm});
            skLineSegment(sketch, "E668", {"start": v(-20.84, 5.71) * mm, "end": v(-20.95, 5.3) * mm});
            skLineSegment(sketch, "E669", {"start": v(-20.95, 5.3) * mm, "end": v(-21.1, 4.72) * mm});
            skLineSegment(sketch, "E670", {"start": v(-21.1, 4.72) * mm, "end": v(-21.37, 2.94) * mm});
            skLineSegment(sketch, "E671", {"start": v(-21.37, 2.94) * mm, "end": v(-21.52, 0.18) * mm});
            skLineSegment(sketch, "E672", {"start": v(-21.52, 0.18) * mm, "end": v(-21.41, -2.57) * mm});
            skLineSegment(sketch, "E673", {"start": v(-21.41, -2.57) * mm, "end": v(-21.18, -4.33) * mm});
            skLineSegment(sketch, "E674", {"start": v(-21.18, -4.33) * mm, "end": v(-21.03, -4.9) * mm});
            skLineSegment(sketch, "E675", {"start": v(-21.03, -4.9) * mm, "end": v(-20.84, -5.65) * mm});
            skLineSegment(sketch, "E676", {"start": v(-20.84, -5.65) * mm, "end": v(-20.06, -7.87) * mm});
            skLineSegment(sketch, "E677", {"start": v(-20.06, -7.87) * mm, "end": v(-18.73, -10.63) * mm});
            skLineSegment(sketch, "E678", {"start": v(-18.73, -10.63) * mm, "end": v(-17.06, -13.15) * mm});
            skLineSegment(sketch, "E679", {"start": v(-17.06, -13.15) * mm, "end": v(-15.1, -15.38) * mm});
            skLineSegment(sketch, "E680", {"start": v(-15.1, -15.38) * mm, "end": v(-12.85, -17.32) * mm});
            skLineSegment(sketch, "E681", {"start": v(-12.85, -17.32) * mm, "end": v(-10.36, -18.93) * mm});
            skLineSegment(sketch, "E682", {"start": v(-10.36, -18.93) * mm, "end": v(-7.66, -20.18) * mm});
            skLineSegment(sketch, "E683", {"start": v(-7.66, -20.18) * mm, "end": v(-5.5, -20.87) * mm});
            skLineSegment(sketch, "E684", {"start": v(-5.5, -20.87) * mm, "end": v(-4.76, -21.03) * mm});
            skLineSegment(sketch, "E685", {"start": v(-4.76, -21.03) * mm, "end": v(-4.5, -21.1) * mm});
            skLineSegment(sketch, "E686", {"start": v(-4.5, -21.1) * mm, "end": v(-3.74, -21.25) * mm});
            skLineSegment(sketch, "E687", {"start": v(-3.74, -21.25) * mm, "end": v(-2.8, -21.4) * mm});
            skLineSegment(sketch, "E688", {"start": v(-2.8, -21.4) * mm, "end": v(-1.76, -21.53) * mm});
            skLineSegment(sketch, "E689", {"start": v(-1.76, -21.53) * mm, "end": v(-0.74, -21.62) * mm});
            skLineSegment(sketch, "E690", {"start": v(-0.74, -21.62) * mm, "end": v(-0.4, -21.64) * mm});
            skLineSegment(sketch, "E691", {"start": v(-0.4, -21.64) * mm, "end": v(-0.33, -21.65) * mm});
            skLineSegment(sketch, "E692", {"start": v(-0.33, -21.65) * mm, "end": v(-0.02, -21.64) * mm});
            skLineSegment(sketch, "E693", {"start": v(-0.02, -21.64) * mm, "end": v(0.61, -21.6) * mm});
            skLineSegment(sketch, "E694", {"start": v(0.61, -21.6) * mm, "end": v(1.4, -21.52) * mm});
            skLineSegment(sketch, "E695", {"start": v(1.4, -21.52) * mm, "end": v(2.06, -21.45) * mm});
            skLineSegment(sketch, "E696", {"start": v(2.06, -21.45) * mm, "end": v(2.28, -21.43) * mm});
            skLineSegment(sketch, "E697", {"start": v(-3.57, -18.34) * mm, "end": v(-3.91, -18.27) * mm});
            skLineSegment(sketch, "E698", {"start": v(-3.91, -18.27) * mm, "end": v(-4.92, -17.96) * mm});
            skLineSegment(sketch, "E699", {"start": v(-4.92, -17.96) * mm, "end": v(-6.57, -17.36) * mm});
            skLineSegment(sketch, "E700", {"start": v(-6.57, -17.36) * mm, "end": v(-8.2, -16.65) * mm});
            skLineSegment(sketch, "E701", {"start": v(-8.2, -16.65) * mm, "end": v(-9.2, -16.17) * mm});
            skLineSegment(sketch, "E702", {"start": v(-9.2, -16.17) * mm, "end": v(-9.53, -15.98) * mm});
            skLineSegment(sketch, "E703", {"start": v(-9.53, -15.98) * mm, "end": v(-10.15, -15.62) * mm});
            skLineSegment(sketch, "E704", {"start": v(-10.15, -15.62) * mm, "end": v(-11.88, -14.3) * mm});
            skLineSegment(sketch, "E705", {"start": v(-11.88, -14.3) * mm, "end": v(-14.05, -12.14) * mm});
            skLineSegment(sketch, "E706", {"start": v(-14.05, -12.14) * mm, "end": v(-15.87, -9.74) * mm});
            skLineSegment(sketch, "E707", {"start": v(-15.87, -9.74) * mm, "end": v(-16.9, -7.92) * mm});
            skLineSegment(sketch, "E708", {"start": v(-16.9, -7.92) * mm, "end": v(-17.15, -7.28) * mm});
            skLineSegment(sketch, "E709", {"start": v(-17.15, -7.28) * mm, "end": v(-17.34, -6.78) * mm});
            skLineSegment(sketch, "E710", {"start": v(-17.34, -6.78) * mm, "end": v(-17.85, -5.26) * mm});
            skLineSegment(sketch, "E711", {"start": v(-17.85, -5.26) * mm, "end": v(-18.28, -3.38) * mm});
            skLineSegment(sketch, "E712", {"start": v(-18.28, -3.38) * mm, "end": v(-18.48, -1.4) * mm});
            skLineSegment(sketch, "E713", {"start": v(-18.48, -1.4) * mm, "end": v(-18.5, 0.33) * mm});
            skLineSegment(sketch, "E714", {"start": v(-18.5, 0.33) * mm, "end": v(-18.47, 0.9) * mm});
            skLineSegment(sketch, "E715", {"start": v(-18.47, 0.9) * mm, "end": v(-18.45, 1.31) * mm});
            skLineSegment(sketch, "E716", {"start": v(-18.45, 1.31) * mm, "end": v(-18.37, 2.56) * mm});
            skLineSegment(sketch, "E717", {"start": v(-18.37, 2.56) * mm, "end": v(-18.23, 3.81) * mm});
            skLineSegment(sketch, "E718", {"start": v(-18.23, 3.81) * mm, "end": v(-18, 4.85) * mm});
            skLineSegment(sketch, "E719", {"start": v(-18, 4.85) * mm, "end": v(-17.77, 5.62) * mm});
            skLineSegment(sketch, "E720", {"start": v(-17.77, 5.62) * mm, "end": v(-17.67, 5.87) * mm});
            skLineSegment(sketch, "E721", {"start": v(-17.67, 5.87) * mm, "end": v(-17.36, 6.72) * mm});
            skLineSegment(sketch, "E722", {"start": v(-17.36, 6.72) * mm, "end": v(-16.1, 9.13) * mm});
            skLineSegment(sketch, "E723", {"start": v(-16.1, 9.13) * mm, "end": v(-13.94, 12.1) * mm});
            skLineSegment(sketch, "E724", {"start": v(-13.94, 12.1) * mm, "end": v(-11.37, 14.6) * mm});
            skLineSegment(sketch, "E725", {"start": v(-11.37, 14.6) * mm, "end": v(-9.27, 16.1) * mm});
            skLineSegment(sketch, "E726", {"start": v(-9.27, 16.1) * mm, "end": v(-8.52, 16.48) * mm});
            skLineSegment(sketch, "E727", {"start": v(-8.52, 16.48) * mm, "end": v(-8.28, 16.61) * mm});
            skLineSegment(sketch, "E728", {"start": v(-8.28, 16.61) * mm, "end": v(-7.56, 16.97) * mm});
            skLineSegment(sketch, "E729", {"start": v(-7.56, 16.97) * mm, "end": v(-6.69, 17.38) * mm});
            skLineSegment(sketch, "E730", {"start": v(-6.69, 17.38) * mm, "end": v(-6, 17.67) * mm});
            skLineSegment(sketch, "E731", {"start": v(-6, 17.67) * mm, "end": v(-5.68, 17.8) * mm});
            skLineSegment(sketch, "E732", {"start": v(-5.68, 17.8) * mm, "end": v(-5.6, 17.8) * mm});
            skLineSegment(sketch, "E733", {"start": v(-5.6, 17.8) * mm, "end": v(-5.54, 17.82) * mm});
            skLineSegment(sketch, "E734", {"start": v(-5.54, 17.82) * mm, "end": v(-5.13, 17.94) * mm});
            skLineSegment(sketch, "E735", {"start": v(-5.13, 17.94) * mm, "end": v(-4.76, 18.11) * mm});
            skLineSegment(sketch, "E736", {"start": v(-4.76, 18.11) * mm, "end": v(-4.71, 18.15) * mm});
            skLineSegment(sketch, "E737", {"start": v(-4.71, 18.15) * mm, "end": v(-4.58, 18.24) * mm});
            skLineSegment(sketch, "E738", {"start": v(-4.58, 18.24) * mm, "end": v(-3.38, 18.38) * mm});
            skLineSegment(sketch, "E739", {"start": v(-3.38, 18.38) * mm, "end": v(-0.83, 18.48) * mm});
            skLineSegment(sketch, "E740", {"start": v(-0.83, 18.48) * mm, "end": v(1.91, 18.45) * mm});
            skLineSegment(sketch, "E741", {"start": v(1.91, 18.45) * mm, "end": v(3.45, 18.35) * mm});
            skLineSegment(sketch, "E742", {"start": v(3.45, 18.35) * mm, "end": v(3.84, 18.26) * mm});
            skLineSegment(sketch, "E743", {"start": v(3.84, 18.26) * mm, "end": v(5.04, 17.98) * mm});
            skLineSegment(sketch, "E744", {"start": v(5.04, 17.98) * mm, "end": v(8.5, 16.55) * mm});
            skLineSegment(sketch, "E745", {"start": v(8.5, 16.55) * mm, "end": v(12.48, 13.75) * mm});
            skLineSegment(sketch, "E746", {"start": v(12.48, 13.75) * mm, "end": v(15.64, 9.96) * mm});
            skLineSegment(sketch, "E747", {"start": v(15.64, 9.96) * mm, "end": v(17.47, 6.5) * mm});
            skLineSegment(sketch, "E748", {"start": v(17.47, 6.5) * mm, "end": v(17.89, 5.3) * mm});
            skLineSegment(sketch, "E749", {"start": v(17.89, 5.3) * mm, "end": v(18.06, 4.77) * mm});
            skLineSegment(sketch, "E750", {"start": v(18.06, 4.77) * mm, "end": v(18.29, 3.05) * mm});
            skLineSegment(sketch, "E751", {"start": v(18.29, 3.05) * mm, "end": v(18.42, 0) * mm});
            skLineSegment(sketch, "E752", {"start": v(18.42, 0) * mm, "end": v(18.29, -3.05) * mm});
            skLineSegment(sketch, "E753", {"start": v(18.29, -3.05) * mm, "end": v(18.06, -4.77) * mm});
            skLineSegment(sketch, "E754", {"start": v(18.06, -4.77) * mm, "end": v(17.89, -5.3) * mm});
            skLineSegment(sketch, "E755", {"start": v(17.89, -5.3) * mm, "end": v(17.57, -6.22) * mm});
            skLineSegment(sketch, "E756", {"start": v(17.57, -6.22) * mm, "end": v(16.3, -8.9) * mm});
            skLineSegment(sketch, "E757", {"start": v(16.3, -8.9) * mm, "end": v(14.16, -12) * mm});
            skLineSegment(sketch, "E758", {"start": v(14.16, -12) * mm, "end": v(11.53, -14.55) * mm});
            skLineSegment(sketch, "E759", {"start": v(11.53, -14.55) * mm, "end": v(9.28, -16.09) * mm});
            skLineSegment(sketch, "E760", {"start": v(9.28, -16.09) * mm, "end": v(8.47, -16.48) * mm});
            skLineSegment(sketch, "E761", {"start": v(8.47, -16.48) * mm, "end": v(7.91, -16.76) * mm});
            skLineSegment(sketch, "E762", {"start": v(7.91, -16.76) * mm, "end": v(6.2, -17.5) * mm});
            skLineSegment(sketch, "E763", {"start": v(6.2, -17.5) * mm, "end": v(4.25, -18.12) * mm});
            skLineSegment(sketch, "E764", {"start": v(4.25, -18.12) * mm, "end": v(2.24, -18.43) * mm});
            skLineSegment(sketch, "E765", {"start": v(2.24, -18.43) * mm, "end": v(0.46, -18.5) * mm});
            skLineSegment(sketch, "E766", {"start": v(0.46, -18.5) * mm, "end": v(-0.13, -18.5) * mm});
            skLineSegment(sketch, "E767", {"start": v(-0.13, -18.5) * mm, "end": v(-0.42, -18.49) * mm});
            skLineSegment(sketch, "E768", {"start": v(-0.42, -18.49) * mm, "end": v(-1.3, -18.47) * mm});
            skLineSegment(sketch, "E769", {"start": v(-1.3, -18.47) * mm, "end": v(-2.34, -18.43) * mm});
            skLineSegment(sketch, "E770", {"start": v(-2.34, -18.43) * mm, "end": v(-3.14, -18.39) * mm});
            skLineSegment(sketch, "E771", {"start": v(-3.14, -18.39) * mm, "end": v(-3.5, -18.36) * mm});
            skLineSegment(sketch, "E772", {"start": v(-3.5, -18.36) * mm, "end": v(-3.57, -18.34) * mm});
            skLineSegment(sketch, "E773", {"start": v(-1.61, -3.57) * mm, "end": v(-1.5, -3.52) * mm});
            skLineSegment(sketch, "E774", {"start": v(-1.5, -3.52) * mm, "end": v(-1.03, -3.12) * mm});
            skLineSegment(sketch, "E775", {"start": v(-1.03, -3.12) * mm, "end": v(-0.72, -2.67) * mm});
            skLineSegment(sketch, "E776", {"start": v(-0.72, -2.67) * mm, "end": v(-0.69, -2.6) * mm});
            skLineSegment(sketch, "E777", {"start": v(-0.69, -2.6) * mm, "end": v(-0.63, -2.36) * mm});
            skLineSegment(sketch, "E778", {"start": v(-0.63, -2.36) * mm, "end": v(-0.53, -1.64) * mm});
            skLineSegment(sketch, "E779", {"start": v(-0.53, -1.64) * mm, "end": v(-0.67, -0.8) * mm});
            skLineSegment(sketch, "E780", {"start": v(-0.67, -0.8) * mm, "end": v(-1.17, 0.15) * mm});
            skLineSegment(sketch, "E781", {"start": v(-1.17, 0.15) * mm, "end": v(-1.87, 1.1) * mm});
            skLineSegment(sketch, "E782", {"start": v(-1.87, 1.1) * mm, "end": v(-2.12, 1.4) * mm});
            skLineSegment(sketch, "E783", {"start": v(-2.12, 1.4) * mm, "end": v(-2.38, 1.73) * mm});
            skLineSegment(sketch, "E784", {"start": v(-2.38, 1.73) * mm, "end": v(-3.11, 2.75) * mm});
            skLineSegment(sketch, "E785", {"start": v(-3.11, 2.75) * mm, "end": v(-3.61, 3.75) * mm});
            skLineSegment(sketch, "E786", {"start": v(-3.61, 3.75) * mm, "end": v(-3.66, 4.52) * mm});
            skLineSegment(sketch, "E787", {"start": v(-3.66, 4.52) * mm, "end": v(-3.4, 5) * mm});
            skLineSegment(sketch, "E788", {"start": v(-3.4, 5) * mm, "end": v(-3.28, 5.13) * mm});
            skLineSegment(sketch, "E789", {"start": v(-3.28, 5.13) * mm, "end": v(-3.15, 5.27) * mm});
            skLineSegment(sketch, "E790", {"start": v(-3.15, 5.27) * mm, "end": v(-2.6, 5.55) * mm});
            skLineSegment(sketch, "E791", {"start": v(-2.6, 5.55) * mm, "end": v(-1.97, 5.46) * mm});
            skLineSegment(sketch, "E792", {"start": v(-1.97, 5.46) * mm, "end": v(-1.5, 4.94) * mm});
            skLineSegment(sketch, "E793", {"start": v(-1.5, 4.94) * mm, "end": v(-1.32, 4.27) * mm});
            skLineSegment(sketch, "E794", {"start": v(-1.32, 4.27) * mm, "end": v(-1.32, 4.05) * mm});
            skLineSegment(sketch, "E795", {"start": v(-1.32, 4.05) * mm, "end": v(-1.32, 3.88) * mm});
            skLineSegment(sketch, "E796", {"start": v(-1.32, 3.88) * mm, "end": v(-1.22, 3.38) * mm});
            skLineSegment(sketch, "E797", {"start": v(-1.22, 3.38) * mm, "end": v(-1, 3.17) * mm});
            skLineSegment(sketch, "E798", {"start": v(-1, 3.17) * mm, "end": v(-0.93, 3.17) * mm});
            skLineSegment(sketch, "E799", {"start": v(-0.93, 3.17) * mm, "end": v(-0.84, 3.17) * mm});
            skLineSegment(sketch, "E800", {"start": v(-0.84, 3.17) * mm, "end": v(-0.57, 3.52) * mm});
            skLineSegment(sketch, "E801", {"start": v(-0.57, 3.52) * mm, "end": v(-0.58, 4.32) * mm});
            skLineSegment(sketch, "E802", {"start": v(-0.58, 4.32) * mm, "end": v(-0.89, 5.22) * mm});
            skLineSegment(sketch, "E803", {"start": v(-0.89, 5.22) * mm, "end": v(-1.26, 5.76) * mm});
            skLineSegment(sketch, "E804", {"start": v(-1.26, 5.76) * mm, "end": v(-1.43, 5.87) * mm});
            skLineSegment(sketch, "E805", {"start": v(-1.43, 5.87) * mm, "end": v(-1.54, 5.94) * mm});
            skLineSegment(sketch, "E806", {"start": v(-1.54, 5.94) * mm, "end": v(-1.95, 6.05) * mm});
            skLineSegment(sketch, "E807", {"start": v(-1.95, 6.05) * mm, "end": v(-2.6, 6.05) * mm});
            skLineSegment(sketch, "E808", {"start": v(-2.6, 6.05) * mm, "end": v(-3.26, 5.91) * mm});
            skLineSegment(sketch, "E809", {"start": v(-3.26, 5.91) * mm, "end": v(-3.65, 5.73) * mm});
            skLineSegment(sketch, "E810", {"start": v(-3.65, 5.73) * mm, "end": v(-3.76, 5.64) * mm});
            skLineSegment(sketch, "E811", {"start": v(-3.76, 5.64) * mm, "end": v(-3.84, 5.56) * mm});
            skLineSegment(sketch, "E812", {"start": v(-3.84, 5.56) * mm, "end": v(-4.11, 5.04) * mm});
            skLineSegment(sketch, "E813", {"start": v(-4.11, 5.04) * mm, "end": v(-4.23, 4.34) * mm});
            skLineSegment(sketch, "E814", {"start": v(-4.23, 4.34) * mm, "end": v(-4.23, 4.1) * mm});
            skLineSegment(sketch, "E815", {"start": v(-4.23, 4.1) * mm, "end": v(-4.23, 3.94) * mm});
            skLineSegment(sketch, "E816", {"start": v(-4.23, 3.94) * mm, "end": v(-4.18, 3.45) * mm});
            skLineSegment(sketch, "E817", {"start": v(-4.18, 3.45) * mm, "end": v(-3.97, 2.86) * mm});
            skLineSegment(sketch, "E818", {"start": v(-3.97, 2.86) * mm, "end": v(-3.53, 2.16) * mm});
            skLineSegment(sketch, "E819", {"start": v(-3.53, 2.16) * mm, "end": v(-2.97, 1.43) * mm});
            skLineSegment(sketch, "E820", {"start": v(-2.97, 1.43) * mm, "end": v(-2.78, 1.2) * mm});
            skLineSegment(sketch, "E821", {"start": v(-2.78, 1.2) * mm, "end": v(-2.6, 0.97) * mm});
            skLineSegment(sketch, "E822", {"start": v(-2.6, 0.97) * mm, "end": v(-2.05, 0.27) * mm});
            skLineSegment(sketch, "E823", {"start": v(-2.05, 0.27) * mm, "end": v(-1.6, -0.42) * mm});
            skLineSegment(sketch, "E824", {"start": v(-1.6, -0.42) * mm, "end": v(-1.38, -1) * mm});
            skLineSegment(sketch, "E825", {"start": v(-1.38, -1) * mm, "end": v(-1.32, -1.42) * mm});
            skLineSegment(sketch, "E826", {"start": v(-1.32, -1.42) * mm, "end": v(-1.32, -1.56) * mm});
            skLineSegment(sketch, "E827", {"start": v(-1.32, -1.56) * mm, "end": v(-1.32, -1.86) * mm});
            skLineSegment(sketch, "E828", {"start": v(-1.32, -1.86) * mm, "end": v(-1.6, -2.76) * mm});
            skLineSegment(sketch, "E829", {"start": v(-1.6, -2.76) * mm, "end": v(-2.2, -3.18) * mm});
            skLineSegment(sketch, "E830", {"start": v(-2.2, -3.18) * mm, "end": v(-2.4, -3.18) * mm});
            skLineSegment(sketch, "E831", {"start": v(-2.4, -3.18) * mm, "end": v(-2.54, -3.18) * mm});
            skLineSegment(sketch, "E832", {"start": v(-2.54, -3.18) * mm, "end": v(-2.92, -3.04) * mm});
            skLineSegment(sketch, "E833", {"start": v(-2.92, -3.04) * mm, "end": v(-3.33, -2.67) * mm});
            skLineSegment(sketch, "E834", {"start": v(-3.33, -2.67) * mm, "end": v(-3.6, -2.11) * mm});
            skLineSegment(sketch, "E835", {"start": v(-3.6, -2.11) * mm, "end": v(-3.7, -1.6) * mm});
            skLineSegment(sketch, "E836", {"start": v(-3.7, -1.6) * mm, "end": v(-3.7, -1.43) * mm});
            skLineSegment(sketch, "E837", {"start": v(-3.7, -1.43) * mm, "end": v(-3.7, -1.27) * mm});
            skLineSegment(sketch, "E838", {"start": v(-3.7, -1.27) * mm, "end": v(-3.78, -0.79) * mm});
            skLineSegment(sketch, "E839", {"start": v(-3.78, -0.79) * mm, "end": v(-3.92, -0.53) * mm});
            skLineSegment(sketch, "E840", {"start": v(-3.92, -0.53) * mm, "end": v(-3.97, -0.53) * mm});
            skLineSegment(sketch, "E841", {"start": v(-3.97, -0.53) * mm, "end": v(-4.01, -0.53) * mm});
            skLineSegment(sketch, "E842", {"start": v(-4.01, -0.53) * mm, "end": v(-4.15, -0.87) * mm});
            skLineSegment(sketch, "E843", {"start": v(-4.15, -0.87) * mm, "end": v(-4.23, -1.47) * mm});
            skLineSegment(sketch, "E844", {"start": v(-4.23, -1.47) * mm, "end": v(-4.23, -1.67) * mm});
            skLineSegment(sketch, "E845", {"start": v(-4.23, -1.67) * mm, "end": v(-4.23, -1.88) * mm});
            skLineSegment(sketch, "E846", {"start": v(-4.23, -1.88) * mm, "end": v(-4.13, -2.52) * mm});
            skLineSegment(sketch, "E847", {"start": v(-4.13, -2.52) * mm, "end": v(-3.81, -3.16) * mm});
            skLineSegment(sketch, "E848", {"start": v(-3.81, -3.16) * mm, "end": v(-3.25, -3.62) * mm});
            skLineSegment(sketch, "E849", {"start": v(-3.25, -3.62) * mm, "end": v(-2.64, -3.88) * mm});
            skLineSegment(sketch, "E850", {"start": v(-2.64, -3.88) * mm, "end": v(-2.43, -3.94) * mm});
            skLineSegment(sketch, "E851", {"start": v(-2.43, -3.94) * mm, "end": v(-2.42, -3.95) * mm});
            skLineSegment(sketch, "E852", {"start": v(-2.42, -3.95) * mm, "end": v(-2.15, -3.85) * mm});
            skLineSegment(sketch, "E853", {"start": v(-2.15, -3.85) * mm, "end": v(-1.71, -3.62) * mm});
            skLineSegment(sketch, "E854", {"start": v(-1.71, -3.62) * mm, "end": v(-1.61, -3.57) * mm});
            skLineSegment(sketch, "E855", {"start": v(-11.38, -3.33) * mm, "end": v(-11.38, -3.26) * mm});
            skLineSegment(sketch, "E856", {"start": v(-11.38, -3.26) * mm, "end": v(-11.63, -3.05) * mm});
            skLineSegment(sketch, "E857", {"start": v(-11.63, -3.05) * mm, "end": v(-12.29, -2.98) * mm});
            skLineSegment(sketch, "E858", {"start": v(-12.29, -2.98) * mm, "end": v(-12.49, -3) * mm});
            skLineSegment(sketch, "E859", {"start": v(-12.49, -3) * mm, "end": v(-13.63, -3.02) * mm});
            skLineSegment(sketch, "E860", {"start": v(-13.63, -3.02) * mm, "end": v(-13.7, 1.56) * mm});
            skLineSegment(sketch, "E861", {"start": v(-13.7, 1.56) * mm, "end": v(-13.71, 2.1) * mm});
            skLineSegment(sketch, "E862", {"start": v(-13.71, 2.1) * mm, "end": v(-13.75, 3.73) * mm});
            skLineSegment(sketch, "E863", {"start": v(-13.75, 3.73) * mm, "end": v(-13.83, 5.12) * mm});
            skLineSegment(sketch, "E864", {"start": v(-13.83, 5.12) * mm, "end": v(-13.94, 5.84) * mm});
            skLineSegment(sketch, "E865", {"start": v(-13.94, 5.84) * mm, "end": v(-14.08, 6.02) * mm});
            skLineSegment(sketch, "E866", {"start": v(-14.08, 6.02) * mm, "end": v(-14.1, 6) * mm});
            skLineSegment(sketch, "E867", {"start": v(-14.1, 6) * mm, "end": v(-14.16, 5.99) * mm});
            skLineSegment(sketch, "E868", {"start": v(-14.16, 5.99) * mm, "end": v(-14.26, 5.7) * mm});
            skLineSegment(sketch, "E869", {"start": v(-14.26, 5.7) * mm, "end": v(-14.37, 4.85) * mm});
            skLineSegment(sketch, "E870", {"start": v(-14.37, 4.85) * mm, "end": v(-14.44, 3.35) * mm});
            skLineSegment(sketch, "E871", {"start": v(-14.44, 3.35) * mm, "end": v(-14.47, 1.67) * mm});
            skLineSegment(sketch, "E872", {"start": v(-14.47, 1.67) * mm, "end": v(-14.47, 1.11) * mm});
            skLineSegment(sketch, "E873", {"start": v(-14.47, 1.11) * mm, "end": v(-14.53, -3.7) * mm});
            skLineSegment(sketch, "E874", {"start": v(-14.53, -3.7) * mm, "end": v(-12.96, -3.7) * mm});
            skLineSegment(sketch, "E875", {"start": v(-12.96, -3.7) * mm, "end": v(-12.78, -3.7) * mm});
            skLineSegment(sketch, "E876", {"start": v(-12.78, -3.7) * mm, "end": v(-12.21, -3.68) * mm});
            skLineSegment(sketch, "E877", {"start": v(-12.21, -3.68) * mm, "end": v(-11.72, -3.62) * mm});
            skLineSegment(sketch, "E878", {"start": v(-11.72, -3.62) * mm, "end": v(-11.46, -3.5) * mm});
            skLineSegment(sketch, "E879", {"start": v(-11.46, -3.5) * mm, "end": v(-11.38, -3.37) * mm});
            skLineSegment(sketch, "E880", {"start": v(-11.38, -3.37) * mm, "end": v(-11.38, -3.33) * mm});
            skLineSegment(sketch, "E881", {"start": v(-7.14, -3.33) * mm, "end": v(-7.14, -3.26) * mm});
            skLineSegment(sketch, "E882", {"start": v(-7.14, -3.26) * mm, "end": v(-7.4, -3.05) * mm});
            skLineSegment(sketch, "E883", {"start": v(-7.4, -3.05) * mm, "end": v(-8.1, -3) * mm});
            skLineSegment(sketch, "E884", {"start": v(-8.1, -3) * mm, "end": v(-8.3, -3.02) * mm});
            skLineSegment(sketch, "E885", {"start": v(-8.3, -3.02) * mm, "end": v(-9.5, -3.07) * mm});
            skLineSegment(sketch, "E886", {"start": v(-9.5, -3.07) * mm, "end": v(-9.58, -1.14) * mm});
            skLineSegment(sketch, "E887", {"start": v(-9.58, -1.14) * mm, "end": v(-9.66, 0.8) * mm});
            skLineSegment(sketch, "E888", {"start": v(-9.66, 0.8) * mm, "end": v(-8.78, 0.8) * mm});
            skLineSegment(sketch, "E889", {"start": v(-8.78, 0.8) * mm, "end": v(-8.62, 0.8) * mm});
            skLineSegment(sketch, "E890", {"start": v(-8.62, 0.8) * mm, "end": v(-8.14, 0.9) * mm});
            skLineSegment(sketch, "E891", {"start": v(-8.14, 0.9) * mm, "end": v(-7.94, 1.12) * mm});
            skLineSegment(sketch, "E892", {"start": v(-7.94, 1.12) * mm, "end": v(-7.94, 1.2) * mm});
            skLineSegment(sketch, "E893", {"start": v(-7.94, 1.2) * mm, "end": v(-7.94, 1.26) * mm});
            skLineSegment(sketch, "E894", {"start": v(-7.94, 1.26) * mm, "end": v(-8.13, 1.49) * mm});
            skLineSegment(sketch, "E895", {"start": v(-8.13, 1.49) * mm, "end": v(-8.56, 1.59) * mm});
            skLineSegment(sketch, "E896", {"start": v(-8.56, 1.59) * mm, "end": v(-8.7, 1.59) * mm});
            skLineSegment(sketch, "E897", {"start": v(-8.7, 1.59) * mm, "end": v(-8.82, 1.59) * mm});
            skLineSegment(sketch, "E898", {"start": v(-8.82, 1.59) * mm, "end": v(-9.15, 1.62) * mm});
            skLineSegment(sketch, "E899", {"start": v(-9.15, 1.62) * mm, "end": v(-9.39, 1.82) * mm});
            skLineSegment(sketch, "E900", {"start": v(-9.39, 1.82) * mm, "end": v(-9.5, 2.37) * mm});
            skLineSegment(sketch, "E901", {"start": v(-9.5, 2.37) * mm, "end": v(-9.56, 3.17) * mm});
            skLineSegment(sketch, "E902", {"start": v(-9.56, 3.17) * mm, "end": v(-9.58, 3.44) * mm});
            skLineSegment(sketch, "E903", {"start": v(-9.58, 3.44) * mm, "end": v(-9.66, 5.27) * mm});
            skLineSegment(sketch, "E904", {"start": v(-9.66, 5.27) * mm, "end": v(-8.5, 5.34) * mm});
            skLineSegment(sketch, "E905", {"start": v(-8.5, 5.34) * mm, "end": v(-8.33, 5.36) * mm});
            skLineSegment(sketch, "E906", {"start": v(-8.33, 5.36) * mm, "end": v(-7.63, 5.5) * mm});
            skLineSegment(sketch, "E907", {"start": v(-7.63, 5.5) * mm, "end": v(-7.22, 5.72) * mm});
            skLineSegment(sketch, "E908", {"start": v(-7.22, 5.72) * mm, "end": v(-7.2, 5.77) * mm});
            skLineSegment(sketch, "E909", {"start": v(-7.2, 5.77) * mm, "end": v(-7.19, 5.8) * mm});
            skLineSegment(sketch, "E910", {"start": v(-7.19, 5.8) * mm, "end": v(-7.22, 5.93) * mm});
            skLineSegment(sketch, "E911", {"start": v(-7.22, 5.93) * mm, "end": v(-7.45, 6.02) * mm});
            skLineSegment(sketch, "E912", {"start": v(-7.45, 6.02) * mm, "end": v(-7.9, 6.05) * mm});
            skLineSegment(sketch, "E913", {"start": v(-7.9, 6.05) * mm, "end": v(-8.44, 6.04) * mm});
            skLineSegment(sketch, "E914", {"start": v(-8.44, 6.04) * mm, "end": v(-8.63, 6.03) * mm});
            skLineSegment(sketch, "E915", {"start": v(-8.63, 6.03) * mm, "end": v(-10.19, 5.95) * mm});
            skLineSegment(sketch, "E916", {"start": v(-10.19, 5.95) * mm, "end": v(-10.27, 1.11) * mm});
            skLineSegment(sketch, "E917", {"start": v(-10.27, 1.11) * mm, "end": v(-10.32, -3.7) * mm});
            skLineSegment(sketch, "E918", {"start": v(-10.32, -3.7) * mm, "end": v(-8.73, -3.7) * mm});
            skLineSegment(sketch, "E919", {"start": v(-8.73, -3.7) * mm, "end": v(-8.54, -3.7) * mm});
            skLineSegment(sketch, "E920", {"start": v(-8.54, -3.7) * mm, "end": v(-7.98, -3.68) * mm});
            skLineSegment(sketch, "E921", {"start": v(-7.98, -3.68) * mm, "end": v(-7.5, -3.62) * mm});
            skLineSegment(sketch, "E922", {"start": v(-7.5, -3.62) * mm, "end": v(-7.23, -3.5) * mm});
            skLineSegment(sketch, "E923", {"start": v(-7.23, -3.5) * mm, "end": v(-7.14, -3.37) * mm});
            skLineSegment(sketch, "E924", {"start": v(-7.14, -3.37) * mm, "end": v(-7.14, -3.33) * mm});
            skLineSegment(sketch, "E925", {"start": v(1.32, -1.59) * mm, "end": v(1.32, 0.53) * mm});
            skLineSegment(sketch, "E926", {"start": v(1.32, 0.53) * mm, "end": v(2.1, 0.53) * mm});
            skLineSegment(sketch, "E927", {"start": v(2.1, 0.53) * mm, "end": v(2.27, 0.53) * mm});
            skLineSegment(sketch, "E928", {"start": v(2.27, 0.53) * mm, "end": v(2.82, 0.69) * mm});
            skLineSegment(sketch, "E929", {"start": v(2.82, 0.69) * mm, "end": v(3.45, 1) * mm});
            skLineSegment(sketch, "E930", {"start": v(3.45, 1) * mm, "end": v(3.55, 1.08) * mm});
            skLineSegment(sketch, "E931", {"start": v(3.55, 1.08) * mm, "end": v(3.64, 1.16) * mm});
            skLineSegment(sketch, "E932", {"start": v(3.64, 1.16) * mm, "end": v(3.9, 1.42) * mm});
            skLineSegment(sketch, "E933", {"start": v(3.9, 1.42) * mm, "end": v(4.12, 1.8) * mm});
            skLineSegment(sketch, "E934", {"start": v(4.12, 1.8) * mm, "end": v(4.21, 2.4) * mm});
            skLineSegment(sketch, "E935", {"start": v(4.21, 2.4) * mm, "end": v(4.23, 3.08) * mm});
            skLineSegment(sketch, "E936", {"start": v(4.23, 3.08) * mm, "end": v(4.23, 3.3) * mm});
            skLineSegment(sketch, "E937", {"start": v(4.23, 3.3) * mm, "end": v(4.23, 3.54) * mm});
            skLineSegment(sketch, "E938", {"start": v(4.23, 3.54) * mm, "end": v(4.21, 4.22) * mm});
            skLineSegment(sketch, "E939", {"start": v(4.21, 4.22) * mm, "end": v(4.12, 4.8) * mm});
            skLineSegment(sketch, "E940", {"start": v(4.12, 4.8) * mm, "end": v(3.9, 5.2) * mm});
            skLineSegment(sketch, "E941", {"start": v(3.9, 5.2) * mm, "end": v(3.64, 5.45) * mm});
            skLineSegment(sketch, "E942", {"start": v(3.64, 5.45) * mm, "end": v(3.55, 5.53) * mm});
            skLineSegment(sketch, "E943", {"start": v(3.55, 5.53) * mm, "end": v(3.43, 5.62) * mm});
            skLineSegment(sketch, "E944", {"start": v(3.43, 5.62) * mm, "end": v(2.75, 5.94) * mm});
            skLineSegment(sketch, "E945", {"start": v(2.75, 5.94) * mm, "end": v(2.06, 6.09) * mm});
            skLineSegment(sketch, "E946", {"start": v(2.06, 6.09) * mm, "end": v(1.83, 6.09) * mm});
            skLineSegment(sketch, "E947", {"start": v(1.83, 6.09) * mm, "end": v(0.8, 6.09) * mm});
            skLineSegment(sketch, "E948", {"start": v(0.8, 6.09) * mm, "end": v(0.8, 1.2) * mm});
            skLineSegment(sketch, "E949", {"start": v(0.8, 1.2) * mm, "end": v(0.8, 0.67) * mm});
            skLineSegment(sketch, "E950", {"start": v(0.8, 0.67) * mm, "end": v(0.81, -0.88) * mm});
            skLineSegment(sketch, "E951", {"start": v(0.81, -0.88) * mm, "end": v(0.87, -2.42) * mm});
            skLineSegment(sketch, "E952", {"start": v(0.87, -2.42) * mm, "end": v(0.95, -3.37) * mm});
            skLineSegment(sketch, "E953", {"start": v(0.95, -3.37) * mm, "end": v(1.03, -3.7) * mm});
            skLineSegment(sketch, "E954", {"start": v(1.03, -3.7) * mm, "end": v(1.06, -3.7) * mm});
            skLineSegment(sketch, "E955", {"start": v(1.06, -3.7) * mm, "end": v(1.08, -3.7) * mm});
            skLineSegment(sketch, "E956", {"start": v(1.08, -3.7) * mm, "end": v(1.17, -3.55) * mm});
            skLineSegment(sketch, "E957", {"start": v(1.17, -3.55) * mm, "end": v(1.25, -3.11) * mm});
            skLineSegment(sketch, "E958", {"start": v(1.25, -3.11) * mm, "end": v(1.3, -2.44) * mm});
            skLineSegment(sketch, "E959", {"start": v(1.3, -2.44) * mm, "end": v(1.32, -1.8) * mm});
            skLineSegment(sketch, "E960", {"start": v(1.32, -1.8) * mm, "end": v(1.32, -1.59) * mm});
            skLineSegment(sketch, "E961", {"start": v(8.52, -3.25) * mm, "end": v(8.6, -3.19) * mm});
            skLineSegment(sketch, "E962", {"start": v(8.6, -3.19) * mm, "end": v(8.77, -2.9) * mm});
            skLineSegment(sketch, "E963", {"start": v(8.77, -2.9) * mm, "end": v(8.92, -2.24) * mm});
            skLineSegment(sketch, "E964", {"start": v(8.92, -2.24) * mm, "end": v(8.98, -0.98) * mm});
            skLineSegment(sketch, "E965", {"start": v(8.98, -0.98) * mm, "end": v(9, 0.6) * mm});
            skLineSegment(sketch, "E966", {"start": v(9, 0.6) * mm, "end": v(9, 1.14) * mm});
            skLineSegment(sketch, "E967", {"start": v(9, 1.14) * mm, "end": v(9, 1.51) * mm});
            skLineSegment(sketch, "E968", {"start": v(9, 1.51) * mm, "end": v(8.98, 2.63) * mm});
            skLineSegment(sketch, "E969", {"start": v(8.98, 2.63) * mm, "end": v(8.94, 3.79) * mm});
            skLineSegment(sketch, "E970", {"start": v(8.94, 3.79) * mm, "end": v(8.86, 4.66) * mm});
            skLineSegment(sketch, "E971", {"start": v(8.86, 4.66) * mm, "end": v(8.72, 5.28) * mm});
            skLineSegment(sketch, "E972", {"start": v(8.72, 5.28) * mm, "end": v(8.5, 5.7) * mm});
            skLineSegment(sketch, "E973", {"start": v(8.5, 5.7) * mm, "end": v(8.21, 5.94) * mm});
            skLineSegment(sketch, "E974", {"start": v(8.21, 5.94) * mm, "end": v(7.82, 6.06) * mm});
            skLineSegment(sketch, "E975", {"start": v(7.82, 6.06) * mm, "end": v(7.45, 6.09) * mm});
            skLineSegment(sketch, "E976", {"start": v(7.45, 6.09) * mm, "end": v(7.33, 6.09) * mm});
            skLineSegment(sketch, "E977", {"start": v(7.33, 6.09) * mm, "end": v(7.2, 6.09) * mm});
            skLineSegment(sketch, "E978", {"start": v(7.2, 6.09) * mm, "end": v(6.79, 6.06) * mm});
            skLineSegment(sketch, "E979", {"start": v(6.79, 6.06) * mm, "end": v(6.37, 5.95) * mm});
            skLineSegment(sketch, "E980", {"start": v(6.37, 5.95) * mm, "end": v(6.06, 5.72) * mm});
            skLineSegment(sketch, "E981", {"start": v(6.06, 5.72) * mm, "end": v(5.84, 5.32) * mm});
            skLineSegment(sketch, "E982", {"start": v(5.84, 5.32) * mm, "end": v(5.7, 4.72) * mm});
            skLineSegment(sketch, "E983", {"start": v(5.7, 4.72) * mm, "end": v(5.6, 3.87) * mm});
            skLineSegment(sketch, "E984", {"start": v(5.6, 3.87) * mm, "end": v(5.57, 2.72) * mm});
            skLineSegment(sketch, "E985", {"start": v(5.57, 2.72) * mm, "end": v(5.56, 1.61) * mm});
            skLineSegment(sketch, "E986", {"start": v(5.56, 1.61) * mm, "end": v(5.56, 1.24) * mm});
            skLineSegment(sketch, "E987", {"start": v(5.56, 1.24) * mm, "end": v(5.56, 0.73) * mm});
            skLineSegment(sketch, "E988", {"start": v(5.56, 0.73) * mm, "end": v(5.57, -0.8) * mm});
            skLineSegment(sketch, "E989", {"start": v(5.57, -0.8) * mm, "end": v(5.64, -2.08) * mm});
            skLineSegment(sketch, "E990", {"start": v(5.64, -2.08) * mm, "end": v(5.78, -2.82) * mm});
            skLineSegment(sketch, "E991", {"start": v(5.78, -2.82) * mm, "end": v(5.93, -3.14) * mm});
            skLineSegment(sketch, "E992", {"start": v(5.93, -3.14) * mm, "end": v(6, -3.23) * mm});
            skLineSegment(sketch, "E993", {"start": v(6, -3.23) * mm, "end": v(6.1, -3.34) * mm});
            skLineSegment(sketch, "E994", {"start": v(6.1, -3.34) * mm, "end": v(6.53, -3.56) * mm});
            skLineSegment(sketch, "E995", {"start": v(6.53, -3.56) * mm, "end": v(7.21, -3.68) * mm});
            skLineSegment(sketch, "E996", {"start": v(7.21, -3.68) * mm, "end": v(7.92, -3.58) * mm});
            skLineSegment(sketch, "E997", {"start": v(7.92, -3.58) * mm, "end": v(8.4, -3.36) * mm});
            skLineSegment(sketch, "E998", {"start": v(8.4, -3.36) * mm, "end": v(8.52, -3.25) * mm});
            skLineSegment(sketch, "E999", {"start": v(12.17, 0.8) * mm, "end": v(12.17, 5.3) * mm});
            skLineSegment(sketch, "E1000", {"start": v(12.17, 5.3) * mm, "end": v(12.83, 5.3) * mm});
            skLineSegment(sketch, "E1001", {"start": v(12.83, 5.3) * mm, "end": v(12.95, 5.3) * mm});
            skLineSegment(sketch, "E1002", {"start": v(12.95, 5.3) * mm, "end": v(13.32, 5.4) * mm});
            skLineSegment(sketch, "E1003", {"start": v(13.32, 5.4) * mm, "end": v(13.5, 5.62) * mm});
            skLineSegment(sketch, "E1004", {"start": v(13.5, 5.62) * mm, "end": v(13.5, 5.69) * mm});
            skLineSegment(sketch, "E1005", {"start": v(13.5, 5.69) * mm, "end": v(13.5, 5.74) * mm});
            skLineSegment(sketch, "E1006", {"start": v(13.5, 5.74) * mm, "end": v(13.43, 5.9) * mm});
            skLineSegment(sketch, "E1007", {"start": v(13.43, 5.9) * mm, "end": v(13.18, 6) * mm});
            skLineSegment(sketch, "E1008", {"start": v(13.18, 6) * mm, "end": v(12.68, 6.05) * mm});
            skLineSegment(sketch, "E1009", {"start": v(12.68, 6.05) * mm, "end": v(12.06, 6.04) * mm});
            skLineSegment(sketch, "E1010", {"start": v(12.06, 6.04) * mm, "end": v(11.85, 6.03) * mm});
            skLineSegment(sketch, "E1011", {"start": v(11.85, 6.03) * mm, "end": v(11.6, 6.02) * mm});
            skLineSegment(sketch, "E1012", {"start": v(11.6, 6.02) * mm, "end": v(10.84, 5.92) * mm});
            skLineSegment(sketch, "E1013", {"start": v(10.84, 5.92) * mm, "end": v(10.31, 5.73) * mm});
            skLineSegment(sketch, "E1014", {"start": v(10.31, 5.73) * mm, "end": v(10.32, 5.5) * mm});
            skLineSegment(sketch, "E1015", {"start": v(10.32, 5.5) * mm, "end": v(10.75, 5.33) * mm});
            skLineSegment(sketch, "E1016", {"start": v(10.75, 5.33) * mm, "end": v(10.9, 5.3) * mm});
            skLineSegment(sketch, "E1017", {"start": v(10.9, 5.3) * mm, "end": v(10.95, 5.28) * mm});
            skLineSegment(sketch, "E1018", {"start": v(10.95, 5.28) * mm, "end": v(11.1, 5.23) * mm});
            skLineSegment(sketch, "E1019", {"start": v(11.1, 5.23) * mm, "end": v(11.25, 5.13) * mm});
            skLineSegment(sketch, "E1020", {"start": v(11.25, 5.13) * mm, "end": v(11.36, 4.93) * mm});
            skLineSegment(sketch, "E1021", {"start": v(11.36, 4.93) * mm, "end": v(11.43, 4.6) * mm});
            skLineSegment(sketch, "E1022", {"start": v(11.43, 4.6) * mm, "end": v(11.48, 4.05) * mm});
            skLineSegment(sketch, "E1023", {"start": v(11.48, 4.05) * mm, "end": v(11.5, 3.26) * mm});
            skLineSegment(sketch, "E1024", {"start": v(11.5, 3.26) * mm, "end": v(11.5, 2.17) * mm});
            skLineSegment(sketch, "E1025", {"start": v(11.5, 2.17) * mm, "end": v(11.5, 1.08) * mm});
            skLineSegment(sketch, "E1026", {"start": v(11.5, 1.08) * mm, "end": v(11.5, 0.71) * mm});
            skLineSegment(sketch, "E1027", {"start": v(11.5, 0.71) * mm, "end": v(11.5, 0.19) * mm});
            skLineSegment(sketch, "E1028", {"start": v(11.5, 0.19) * mm, "end": v(11.53, -1.4) * mm});
            skLineSegment(sketch, "E1029", {"start": v(11.53, -1.4) * mm, "end": v(11.58, -2.75) * mm});
            skLineSegment(sketch, "E1030", {"start": v(11.58, -2.75) * mm, "end": v(11.69, -3.49) * mm});
            skLineSegment(sketch, "E1031", {"start": v(11.69, -3.49) * mm, "end": v(11.81, -3.7) * mm});
            skLineSegment(sketch, "E1032", {"start": v(11.81, -3.7) * mm, "end": v(11.85, -3.7) * mm});
            skLineSegment(sketch, "E1033", {"start": v(11.85, -3.7) * mm, "end": v(11.9, -3.7) * mm});
            skLineSegment(sketch, "E1034", {"start": v(11.9, -3.7) * mm, "end": v(12, -3.48) * mm});
            skLineSegment(sketch, "E1035", {"start": v(12, -3.48) * mm, "end": v(12.1, -2.73) * mm});
            skLineSegment(sketch, "E1036", {"start": v(12.1, -2.73) * mm, "end": v(12.15, -1.35) * mm});
            skLineSegment(sketch, "E1037", {"start": v(12.15, -1.35) * mm, "end": v(12.17, 0.26) * mm});
            skLineSegment(sketch, "E1038", {"start": v(12.17, 0.26) * mm, "end": v(12.17, 0.8) * mm});
            skLineSegment(sketch, "E1039", {"start": v(15.08, 5.3) * mm, "end": v(15.08, 5.43) * mm});
            skLineSegment(sketch, "E1040", {"start": v(15.08, 5.43) * mm, "end": v(15, 5.85) * mm});
            skLineSegment(sketch, "E1041", {"start": v(15, 5.85) * mm, "end": v(14.86, 6.09) * mm});
            skLineSegment(sketch, "E1042", {"start": v(14.86, 6.09) * mm, "end": v(14.82, 6.09) * mm});
            skLineSegment(sketch, "E1043", {"start": v(14.82, 6.09) * mm, "end": v(14.77, 6.09) * mm});
            skLineSegment(sketch, "E1044", {"start": v(14.77, 6.09) * mm, "end": v(14.64, 5.85) * mm});
            skLineSegment(sketch, "E1045", {"start": v(14.64, 5.85) * mm, "end": v(14.6, 5.4) * mm});
            skLineSegment(sketch, "E1046", {"start": v(14.6, 5.4) * mm, "end": v(14.6, 5.3) * mm});
            skLineSegment(sketch, "E1047", {"start": v(14.6, 5.3) * mm, "end": v(14.61, 5.18) * mm});
            skLineSegment(sketch, "E1048", {"start": v(14.61, 5.18) * mm, "end": v(14.7, 4.73) * mm});
            skLineSegment(sketch, "E1049", {"start": v(14.7, 4.73) * mm, "end": v(14.83, 4.5) * mm});
            skLineSegment(sketch, "E1050", {"start": v(14.83, 4.5) * mm, "end": v(14.87, 4.5) * mm});
            skLineSegment(sketch, "E1051", {"start": v(14.87, 4.5) * mm, "end": v(14.9, 4.5) * mm});
            skLineSegment(sketch, "E1052", {"start": v(14.9, 4.5) * mm, "end": v(15.01, 4.73) * mm});
            skLineSegment(sketch, "E1053", {"start": v(15.01, 4.73) * mm, "end": v(15.08, 5.15) * mm});
            skLineSegment(sketch, "E1054", {"start": v(15.08, 5.15) * mm, "end": v(15.08, 5.3) * mm});
            skLineSegment(sketch, "E1055", {"start": v(1.32, 3.3) * mm, "end": v(1.32, 5.3) * mm});
            skLineSegment(sketch, "E1056", {"start": v(1.32, 5.3) * mm, "end": v(2.1, 5.3) * mm});
            skLineSegment(sketch, "E1057", {"start": v(2.1, 5.3) * mm, "end": v(2.27, 5.3) * mm});
            skLineSegment(sketch, "E1058", {"start": v(2.27, 5.3) * mm, "end": v(2.8, 5.17) * mm});
            skLineSegment(sketch, "E1059", {"start": v(2.8, 5.17) * mm, "end": v(3.3, 4.82) * mm});
            skLineSegment(sketch, "E1060", {"start": v(3.3, 4.82) * mm, "end": v(3.6, 4.23) * mm});
            skLineSegment(sketch, "E1061", {"start": v(3.6, 4.23) * mm, "end": v(3.7, 3.62) * mm});
            skLineSegment(sketch, "E1062", {"start": v(3.7, 3.62) * mm, "end": v(3.7, 3.41) * mm});
            skLineSegment(sketch, "E1063", {"start": v(3.7, 3.41) * mm, "end": v(3.7, 3.17) * mm});
            skLineSegment(sketch, "E1064", {"start": v(3.7, 3.17) * mm, "end": v(3.63, 2.43) * mm});
            skLineSegment(sketch, "E1065", {"start": v(3.63, 2.43) * mm, "end": v(3.38, 1.78) * mm});
            skLineSegment(sketch, "E1066", {"start": v(3.38, 1.78) * mm, "end": v(2.93, 1.43) * mm});
            skLineSegment(sketch, "E1067", {"start": v(2.93, 1.43) * mm, "end": v(2.42, 1.32) * mm});
            skLineSegment(sketch, "E1068", {"start": v(2.42, 1.32) * mm, "end": v(2.25, 1.32) * mm});
            skLineSegment(sketch, "E1069", {"start": v(2.25, 1.32) * mm, "end": v(1.32, 1.32) * mm});
            skLineSegment(sketch, "E1070", {"start": v(1.32, 1.32) * mm, "end": v(1.32, 3.3) * mm});
            skLineSegment(sketch, "E1071", {"start": v(6.88, -3.15) * mm, "end": v(6.88, -3.1) * mm});
            skLineSegment(sketch, "E1072", {"start": v(6.88, -3.1) * mm, "end": v(6.78, -2.98) * mm});
            skLineSegment(sketch, "E1073", {"start": v(6.78, -2.98) * mm, "end": v(6.62, -2.91) * mm});
            skLineSegment(sketch, "E1074", {"start": v(6.62, -2.91) * mm, "end": v(6.56, -2.91) * mm});
            skLineSegment(sketch, "E1075", {"start": v(6.56, -2.91) * mm, "end": v(6.52, -2.91) * mm});
            skLineSegment(sketch, "E1076", {"start": v(6.52, -2.91) * mm, "end": v(6.4, -2.73) * mm});
            skLineSegment(sketch, "E1077", {"start": v(6.4, -2.73) * mm, "end": v(6.3, -2.13) * mm});
            skLineSegment(sketch, "E1078", {"start": v(6.3, -2.13) * mm, "end": v(6.28, -1.01) * mm});
            skLineSegment(sketch, "E1079", {"start": v(6.28, -1.01) * mm, "end": v(6.29, 0.28) * mm});
            skLineSegment(sketch, "E1080", {"start": v(6.29, 0.28) * mm, "end": v(6.3, 0.71) * mm});
            skLineSegment(sketch, "E1081", {"start": v(6.3, 0.71) * mm, "end": v(6.3, 1.08) * mm});
            skLineSegment(sketch, "E1082", {"start": v(6.3, 1.08) * mm, "end": v(6.33, 2.18) * mm});
            skLineSegment(sketch, "E1083", {"start": v(6.33, 2.18) * mm, "end": v(6.37, 3.31) * mm});
            skLineSegment(sketch, "E1084", {"start": v(6.37, 3.31) * mm, "end": v(6.42, 4.17) * mm});
            skLineSegment(sketch, "E1085", {"start": v(6.42, 4.17) * mm, "end": v(6.5, 4.77) * mm});
            skLineSegment(sketch, "E1086", {"start": v(6.5, 4.77) * mm, "end": v(6.6, 5.18) * mm});
            skLineSegment(sketch, "E1087", {"start": v(6.6, 5.18) * mm, "end": v(6.73, 5.41) * mm});
            skLineSegment(sketch, "E1088", {"start": v(6.73, 5.41) * mm, "end": v(6.91, 5.53) * mm});
            skLineSegment(sketch, "E1089", {"start": v(6.91, 5.53) * mm, "end": v(7.09, 5.56) * mm});
            skLineSegment(sketch, "E1090", {"start": v(7.09, 5.56) * mm, "end": v(7.14, 5.56) * mm});
            skLineSegment(sketch, "E1091", {"start": v(7.14, 5.56) * mm, "end": v(7.27, 5.56) * mm});
            skLineSegment(sketch, "E1092", {"start": v(7.27, 5.56) * mm, "end": v(7.67, 5.36) * mm});
            skLineSegment(sketch, "E1093", {"start": v(7.67, 5.36) * mm, "end": v(7.99, 4.67) * mm});
            skLineSegment(sketch, "E1094", {"start": v(7.99, 4.67) * mm, "end": v(8.16, 3.3) * mm});
            skLineSegment(sketch, "E1095", {"start": v(8.16, 3.3) * mm, "end": v(8.2, 1.64) * mm});
            skLineSegment(sketch, "E1096", {"start": v(8.2, 1.64) * mm, "end": v(8.2, 1.08) * mm});
            skLineSegment(sketch, "E1097", {"start": v(8.2, 1.08) * mm, "end": v(8.2, 0.7) * mm});
            skLineSegment(sketch, "E1098", {"start": v(8.2, 0.7) * mm, "end": v(8.22, -0.42) * mm});
            skLineSegment(sketch, "E1099", {"start": v(8.22, -0.42) * mm, "end": v(8.28, -1.5) * mm});
            skLineSegment(sketch, "E1100", {"start": v(8.28, -1.5) * mm, "end": v(8.37, -2.16) * mm});
            skLineSegment(sketch, "E1101", {"start": v(8.4, -2.37) * mm, "end": v(8.38, -2.56) * mm});
            skLineSegment(sketch, "E1102", {"start": v(6.88, -3.18) * mm, "end": v(6.88, -3.15) * mm});
            skSolve(sketch);
        }
        {
            var Q0;
            Q0=makeQuery(id+"F0.imprint","IMPRINT",FACE,{"disambiguationData":[TD([[makeQuery(id+"F0.imprint","IMPRINT",EDGE,{"derivedFrom":sQuery(id+"F0.wireOp",EDGE,"E132")}),-1.0]])]});
            var Q1;
            Q1=makeQuery(id+"F0.imprint","IMPRINT",FACE,{"disambiguationData":[TD([[makeQuery(id+"F0.imprint","IMPRINT",EDGE,{"derivedFrom":sQuery(id+"F0.wireOp",EDGE,"E855")}),1.0]])]});
            var Q2;
            Q2=makeQuery(id+"F0.imprint","IMPRINT",FACE,{"disambiguationData":[TD([[makeQuery(id+"F0.imprint","IMPRINT",EDGE,{"derivedFrom":sQuery(id+"F0.wireOp",EDGE,"E881")}),1.0]])]});
            var Q3;
            {var subQ10=sQuery(id+"F0.wireOp",EDGE,"E288");Q3=makeQuery(id+"F0.imprint","IMPRINT",FACE,{"disambiguationData":[TD([[makeQuery(id+"F0.imprint","IMPRINT",EDGE,{"derivedFrom":subQ10}),-1.0]])]});}
            var Q4;
            {var subQ1=sQuery(id+"F0.wireOp",EDGE,"E402");Q4=makeQuery(id+"F0.imprint","IMPRINT",FACE,{"disambiguationData":[TD([[makeQuery(id+"F0.imprint","IMPRINT",EDGE,{"derivedFrom":subQ1}),-1.0]])]});}
            var Q5;
            Q5=makeQuery(id+"F0.imprint","IMPRINT",FACE,{"disambiguationData":[TD([[makeQuery(id+"F0.imprint","IMPRINT",EDGE,{"derivedFrom":sQuery(id+"F0.wireOp",EDGE,"E457")}),-1.0]])]});
            var Q6;
            Q6=makeQuery(id+"F0.imprint","IMPRINT",FACE,{"disambiguationData":[TD([[makeQuery(id+"F0.imprint","IMPRINT",EDGE,{"derivedFrom":sQuery(id+"F0.wireOp",EDGE,"E999")}),1.0]])]});
            var Q7;
            Q7=makeQuery(id+"F0.imprint","IMPRINT",FACE,{"disambiguationData":[TD([[makeQuery(id+"F0.imprint","IMPRINT",EDGE,{"derivedFrom":sQuery(id+"F0.wireOp",EDGE,"E1039")}),1.0]])]});
            extrude(context, id + "F1", {"entities" : qUnion([Q0, Q1, Q2, Q3, Q4, Q5, Q6, Q7]), "depth" : 3 * mm});
        }
        {
            var Q0;
            Q0=makeQuery(id+"F1.opExtrude","CAP_FACE",FACE,{"disambiguationData":[OSD([sQuery(id+"F0.wireOp",EDGE,"E2"),sQuery(id+"F0.wireOp",EDGE,"E3"),sQuery(id+"F0.wireOp",EDGE,"E4"),sQuery(id+"F0.wireOp",EDGE,"E5"),sQuery(id+"F0.wireOp",EDGE,"E6"),sQuery(id+"F0.wireOp",EDGE,"E7"),sQuery(id+"F0.wireOp",EDGE,"E8"),sQuery(id+"F0.wireOp",EDGE,"E109"),sQuery(id+"F0.wireOp",EDGE,"E110"),sQuery(id+"F0.wireOp",EDGE,"E111"),sQuery(id+"F0.wireOp",EDGE,"E112"),sQuery(id+"F0.wireOp",EDGE,"E116"),sQuery(id+"F0.wireOp",EDGE,"E117"),sQuery(id+"F0.wireOp",EDGE,"E121"),sQuery(id+"F0.wireOp",EDGE,"E122"),sQuery(id+"F0.wireOp",EDGE,"E123"),sQuery(id+"F0.wireOp",EDGE,"E128"),sQuery(id+"F0.wireOp",EDGE,"E129"),sQuery(id+"F0.wireOp",EDGE,"E132"),sQuery(id+"F0.wireOp",EDGE,"E133"),sQuery(id+"F0.wireOp",EDGE,"E134"),sQuery(id+"F0.wireOp",EDGE,"E136"),sQuery(id+"F0.wireOp",EDGE,"E137"),sQuery(id+"F0.wireOp",EDGE,"E138"),sQuery(id+"F0.wireOp",EDGE,"E139"),sQuery(id+"F0.wireOp",EDGE,"E140"),sQuery(id+"F0.wireOp",EDGE,"E141"),sQuery(id+"F0.wireOp",EDGE,"E206"),sQuery(id+"F0.wireOp",EDGE,"E207"),sQuery(id+"F0.wireOp",EDGE,"E208"),sQuery(id+"F0.wireOp",EDGE,"E210"),sQuery(id+"F0.wireOp",EDGE,"E211"),sQuery(id+"F0.wireOp",EDGE,"E556"),sQuery(id+"F0.wireOp",EDGE,"E557"),sQuery(id+"F0.wireOp",EDGE,"E560"),sQuery(id+"F0.wireOp",EDGE,"E561"),sQuery(id+"F0.wireOp",EDGE,"E562"),sQuery(id+"F0.wireOp",EDGE,"E563"),sQuery(id+"F0.wireOp",EDGE,"E566"),sQuery(id+"F0.wireOp",EDGE,"E567"),sQuery(id+"F0.wireOp",EDGE,"E569"),sQuery(id+"F0.wireOp",EDGE,"E572"),sQuery(id+"F0.wireOp",EDGE,"E574"),sQuery(id+"F0.wireOp",EDGE,"E575"),sQuery(id+"F0.wireOp",EDGE,"E576"),sQuery(id+"F0.wireOp",EDGE,"E577"),sQuery(id+"F0.wireOp",EDGE,"E578"),sQuery(id+"F0.wireOp",EDGE,"E579"),sQuery(id+"F0.wireOp",EDGE,"E580"),sQuery(id+"F0.wireOp",EDGE,"E581"),sQuery(id+"F0.wireOp",EDGE,"E582"),sQuery(id+"F0.wireOp",EDGE,"E583"),sQuery(id+"F0.wireOp",EDGE,"E584"),sQuery(id+"F0.wireOp",EDGE,"E585"),sQuery(id+"F0.wireOp",EDGE,"E586"),sQuery(id+"F0.wireOp",EDGE,"E587"),sQuery(id+"F0.wireOp",EDGE,"E588"),sQuery(id+"F0.wireOp",EDGE,"E589"),sQuery(id+"F0.wireOp",EDGE,"E590"),sQuery(id+"F0.wireOp",EDGE,"E591"),sQuery(id+"F0.wireOp",EDGE,"E592"),sQuery(id+"F0.wireOp",EDGE,"E593"),sQuery(id+"F0.wireOp",EDGE,"E594"),sQuery(id+"F0.wireOp",EDGE,"E595"),sQuery(id+"F0.wireOp",EDGE,"E596"),sQuery(id+"F0.wireOp",EDGE,"E597"),sQuery(id+"F0.wireOp",EDGE,"E598"),sQuery(id+"F0.wireOp",EDGE,"E599"),sQuery(id+"F0.wireOp",EDGE,"E600"),sQuery(id+"F0.wireOp",EDGE,"E601"),sQuery(id+"F0.wireOp",EDGE,"E602"),sQuery(id+"F0.wireOp",EDGE,"E603"),sQuery(id+"F0.wireOp",EDGE,"E604"),sQuery(id+"F0.wireOp",EDGE,"E605"),sQuery(id+"F0.wireOp",EDGE,"E606"),sQuery(id+"F0.wireOp",EDGE,"E607"),sQuery(id+"F0.wireOp",EDGE,"E608"),sQuery(id+"F0.wireOp",EDGE,"E609"),sQuery(id+"F0.wireOp",EDGE,"E610"),sQuery(id+"F0.wireOp",EDGE,"E611"),sQuery(id+"F0.wireOp",EDGE,"E612"),sQuery(id+"F0.wireOp",EDGE,"E613"),sQuery(id+"F0.wireOp",EDGE,"E614"),sQuery(id+"F0.wireOp",EDGE,"E615"),sQuery(id+"F0.wireOp",EDGE,"E616"),sQuery(id+"F0.wireOp",EDGE,"E617"),sQuery(id+"F0.wireOp",EDGE,"E618"),sQuery(id+"F0.wireOp",EDGE,"E619"),sQuery(id+"F0.wireOp",EDGE,"E620"),sQuery(id+"F0.wireOp",EDGE,"E621"),sQuery(id+"F0.wireOp",EDGE,"E622"),sQuery(id+"F0.wireOp",EDGE,"E623"),sQuery(id+"F0.wireOp",EDGE,"E624"),sQuery(id+"F0.wireOp",EDGE,"E625"),sQuery(id+"F0.wireOp",EDGE,"E626"),sQuery(id+"F0.wireOp",EDGE,"E627"),sQuery(id+"F0.wireOp",EDGE,"E628"),sQuery(id+"F0.wireOp",EDGE,"E629"),sQuery(id+"F0.wireOp",EDGE,"E630"),sQuery(id+"F0.wireOp",EDGE,"E631"),sQuery(id+"F0.wireOp",EDGE,"E632"),sQuery(id+"F0.wireOp",EDGE,"E633"),sQuery(id+"F0.wireOp",EDGE,"E634"),sQuery(id+"F0.wireOp",EDGE,"E635"),sQuery(id+"F0.wireOp",EDGE,"E636"),sQuery(id+"F0.wireOp",EDGE,"E637"),sQuery(id+"F0.wireOp",EDGE,"E638"),sQuery(id+"F0.wireOp",EDGE,"E639"),sQuery(id+"F0.wireOp",EDGE,"E640"),sQuery(id+"F0.wireOp",EDGE,"E641"),sQuery(id+"F0.wireOp",EDGE,"E642"),sQuery(id+"F0.wireOp",EDGE,"E643"),sQuery(id+"F0.wireOp",EDGE,"E644"),sQuery(id+"F0.wireOp",EDGE,"E645"),sQuery(id+"F0.wireOp",EDGE,"E646"),sQuery(id+"F0.wireOp",EDGE,"E647"),sQuery(id+"F0.wireOp",EDGE,"E648"),sQuery(id+"F0.wireOp",EDGE,"E649"),sQuery(id+"F0.wireOp",EDGE,"E650"),sQuery(id+"F0.wireOp",EDGE,"E651"),sQuery(id+"F0.wireOp",EDGE,"E652"),sQuery(id+"F0.wireOp",EDGE,"E653"),sQuery(id+"F0.wireOp",EDGE,"E654"),sQuery(id+"F0.wireOp",EDGE,"E655"),sQuery(id+"F0.wireOp",EDGE,"E656"),sQuery(id+"F0.wireOp",EDGE,"E657"),sQuery(id+"F0.wireOp",EDGE,"E658"),sQuery(id+"F0.wireOp",EDGE,"E659"),sQuery(id+"F0.wireOp",EDGE,"E660"),sQuery(id+"F0.wireOp",EDGE,"E661"),sQuery(id+"F0.wireOp",EDGE,"E662"),sQuery(id+"F0.wireOp",EDGE,"E663"),sQuery(id+"F0.wireOp",EDGE,"E664"),sQuery(id+"F0.wireOp",EDGE,"E665"),sQuery(id+"F0.wireOp",EDGE,"E666"),sQuery(id+"F0.wireOp",EDGE,"E667"),sQuery(id+"F0.wireOp",EDGE,"E668"),sQuery(id+"F0.wireOp",EDGE,"E669"),sQuery(id+"F0.wireOp",EDGE,"E670"),sQuery(id+"F0.wireOp",EDGE,"E671"),sQuery(id+"F0.wireOp",EDGE,"E672"),sQuery(id+"F0.wireOp",EDGE,"E673"),sQuery(id+"F0.wireOp",EDGE,"E674"),sQuery(id+"F0.wireOp",EDGE,"E675"),sQuery(id+"F0.wireOp",EDGE,"E676"),sQuery(id+"F0.wireOp",EDGE,"E677"),sQuery(id+"F0.wireOp",EDGE,"E678"),sQuery(id+"F0.wireOp",EDGE,"E679"),sQuery(id+"F0.wireOp",EDGE,"E680"),sQuery(id+"F0.wireOp",EDGE,"E681"),sQuery(id+"F0.wireOp",EDGE,"E682"),sQuery(id+"F0.wireOp",EDGE,"E683"),sQuery(id+"F0.wireOp",EDGE,"E684"),sQuery(id+"F0.wireOp",EDGE,"E685"),sQuery(id+"F0.wireOp",EDGE,"E686"),sQuery(id+"F0.wireOp",EDGE,"E687"),sQuery(id+"F0.wireOp",EDGE,"E688"),sQuery(id+"F0.wireOp",EDGE,"E689"),sQuery(id+"F0.wireOp",EDGE,"E691"),sQuery(id+"F0.wireOp",EDGE,"E692"),sQuery(id+"F0.wireOp",EDGE,"E693"),sQuery(id+"F0.wireOp",EDGE,"E694"),sQuery(id+"F0.wireOp",EDGE,"E697"),sQuery(id+"F0.wireOp",EDGE,"E698"),sQuery(id+"F0.wireOp",EDGE,"E699"),sQuery(id+"F0.wireOp",EDGE,"E700"),sQuery(id+"F0.wireOp",EDGE,"E701"),sQuery(id+"F0.wireOp",EDGE,"E702"),sQuery(id+"F0.wireOp",EDGE,"E703"),sQuery(id+"F0.wireOp",EDGE,"E704"),sQuery(id+"F0.wireOp",EDGE,"E705"),sQuery(id+"F0.wireOp",EDGE,"E706"),sQuery(id+"F0.wireOp",EDGE,"E707"),sQuery(id+"F0.wireOp",EDGE,"E708"),sQuery(id+"F0.wireOp",EDGE,"E709"),sQuery(id+"F0.wireOp",EDGE,"E710"),sQuery(id+"F0.wireOp",EDGE,"E711"),sQuery(id+"F0.wireOp",EDGE,"E712"),sQuery(id+"F0.wireOp",EDGE,"E713"),sQuery(id+"F0.wireOp",EDGE,"E714"),sQuery(id+"F0.wireOp",EDGE,"E715"),sQuery(id+"F0.wireOp",EDGE,"E716"),sQuery(id+"F0.wireOp",EDGE,"E717"),sQuery(id+"F0.wireOp",EDGE,"E718"),sQuery(id+"F0.wireOp",EDGE,"E719"),sQuery(id+"F0.wireOp",EDGE,"E720"),sQuery(id+"F0.wireOp",EDGE,"E721"),sQuery(id+"F0.wireOp",EDGE,"E722"),sQuery(id+"F0.wireOp",EDGE,"E723"),sQuery(id+"F0.wireOp",EDGE,"E724"),sQuery(id+"F0.wireOp",EDGE,"E725"),sQuery(id+"F0.wireOp",EDGE,"E726"),sQuery(id+"F0.wireOp",EDGE,"E727"),sQuery(id+"F0.wireOp",EDGE,"E728"),sQuery(id+"F0.wireOp",EDGE,"E729"),sQuery(id+"F0.wireOp",EDGE,"E730"),sQuery(id+"F0.wireOp",EDGE,"E731"),sQuery(id+"F0.wireOp",EDGE,"E732"),sQuery(id+"F0.wireOp",EDGE,"E733"),sQuery(id+"F0.wireOp",EDGE,"E734"),sQuery(id+"F0.wireOp",EDGE,"E735"),sQuery(id+"F0.wireOp",EDGE,"E736"),sQuery(id+"F0.wireOp",EDGE,"E737"),sQuery(id+"F0.wireOp",EDGE,"E738"),sQuery(id+"F0.wireOp",EDGE,"E739"),sQuery(id+"F0.wireOp",EDGE,"E740"),sQuery(id+"F0.wireOp",EDGE,"E741"),sQuery(id+"F0.wireOp",EDGE,"E742"),sQuery(id+"F0.wireOp",EDGE,"E743"),sQuery(id+"F0.wireOp",EDGE,"E744"),sQuery(id+"F0.wireOp",EDGE,"E745"),sQuery(id+"F0.wireOp",EDGE,"E746"),sQuery(id+"F0.wireOp",EDGE,"E747"),sQuery(id+"F0.wireOp",EDGE,"E748"),sQuery(id+"F0.wireOp",EDGE,"E749"),sQuery(id+"F0.wireOp",EDGE,"E750"),sQuery(id+"F0.wireOp",EDGE,"E751"),sQuery(id+"F0.wireOp",EDGE,"E752"),sQuery(id+"F0.wireOp",EDGE,"E753"),sQuery(id+"F0.wireOp",EDGE,"E754"),sQuery(id+"F0.wireOp",EDGE,"E755"),sQuery(id+"F0.wireOp",EDGE,"E756"),sQuery(id+"F0.wireOp",EDGE,"E757"),sQuery(id+"F0.wireOp",EDGE,"E758"),sQuery(id+"F0.wireOp",EDGE,"E759"),sQuery(id+"F0.wireOp",EDGE,"E760"),sQuery(id+"F0.wireOp",EDGE,"E761"),sQuery(id+"F0.wireOp",EDGE,"E762"),sQuery(id+"F0.wireOp",EDGE,"E763"),sQuery(id+"F0.wireOp",EDGE,"E764"),sQuery(id+"F0.wireOp",EDGE,"E765"),sQuery(id+"F0.wireOp",EDGE,"E766"),sQuery(id+"F0.wireOp",EDGE,"E767"),sQuery(id+"F0.wireOp",EDGE,"E768"),sQuery(id+"F0.wireOp",EDGE,"E771"),sQuery(id+"F0.wireOp",EDGE,"E772")])],"isStart":false});
            var sketch = newSketch(context, id + "F2", { "sketchPlane" : qUnion([Q0])});
            skCircle(sketch, "E1103", {"center": v(-0.84, 0) * mm, "radius": 28.08 * mm});
            skSolve(sketch);
        }
        {
            var Q0;
            Q0=makeQuery(id+"F2.imprint","IMPRINT",FACE,{"disambiguationData":[TD([[makeQuery(id+"F2.imprint","IMPRINT",EDGE,{"derivedFrom":makeQuery(id+"F1.opExtrude","CAP_EDGE",EDGE,{"disambiguationData":[OSD([sQuery(id+"F0.wireOp",EDGE,"E136")])],"isStart":false})}),1.0]])]});
            var Q1;
            Q1=makeQuery(id+"F2.imprint","IMPRINT",FACE,{"disambiguationData":[TD([[makeQuery(id+"F2.imprint","IMPRINT",EDGE,{"derivedFrom":makeQuery(id+"F1.opExtrude","CAP_EDGE",EDGE,{"disambiguationData":[OSD([sQuery(id+"F0.wireOp",EDGE,"E2")])],"isStart":false})}),-1.0]])]});
            var Q2;
            Q2=makeQuery(id+"F2.imprint","IMPRINT",FACE,{"disambiguationData":[TD([[makeQuery(id+"F2.imprint","IMPRINT",EDGE,{"derivedFrom":sQuery(id+"F2.wireOp",EDGE,"E1103")}),1.0]])]});
            extrude(context, id + "F3", {"entities" : qUnion([Q0, Q1, Q2]), "depth" : 40 * mm});
        }
    });
